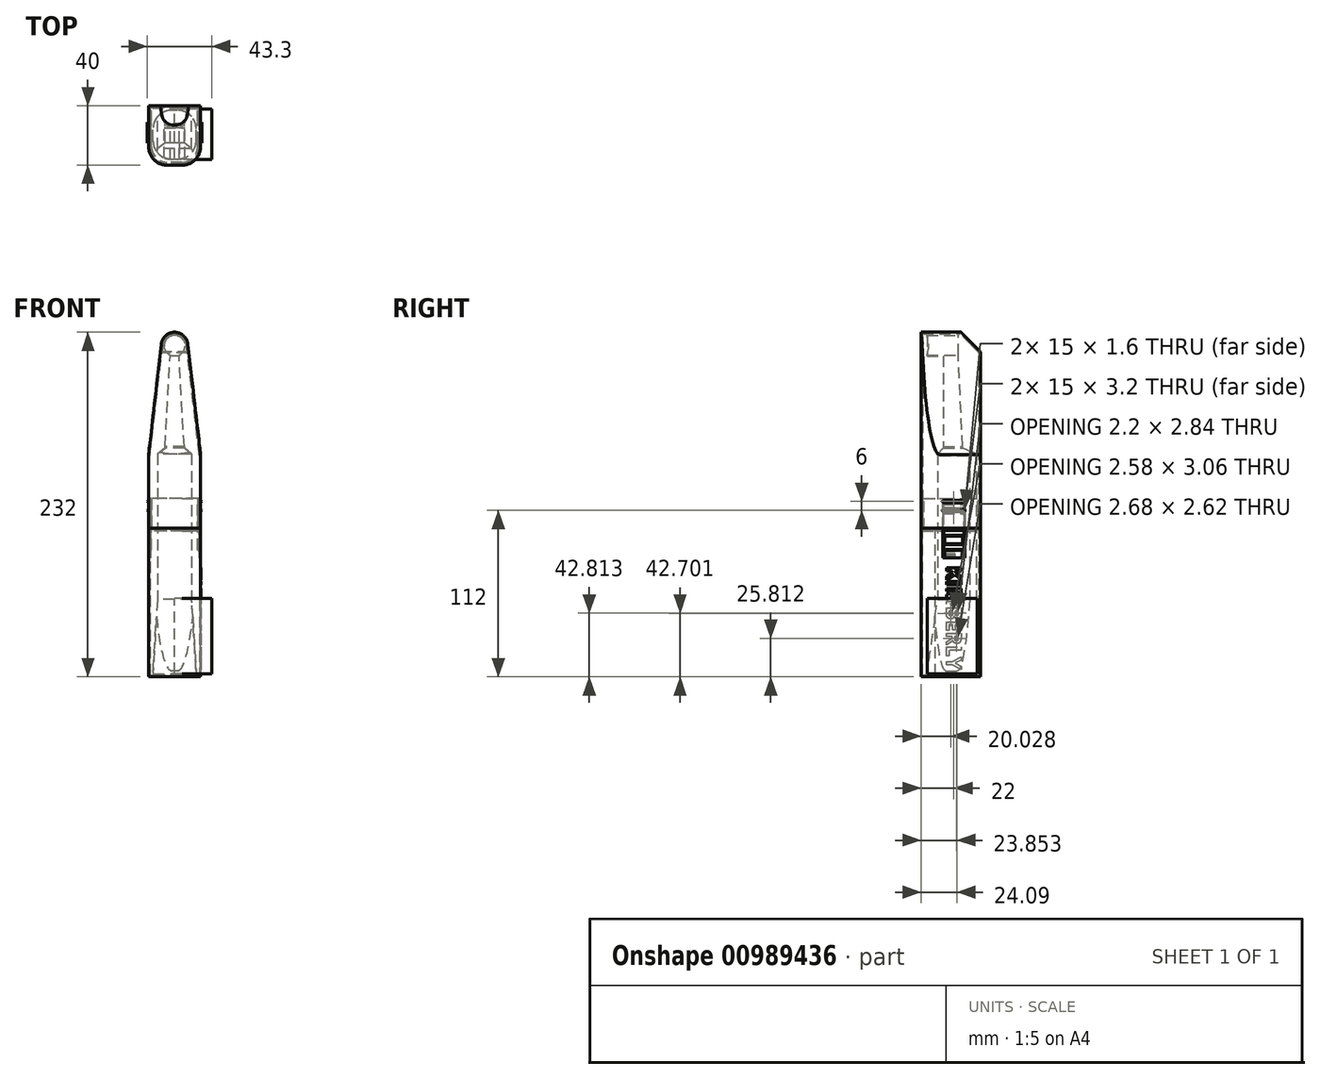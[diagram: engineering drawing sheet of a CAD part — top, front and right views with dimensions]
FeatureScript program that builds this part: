
annotation { "Feature Type Name" : "Feature", "Feature Type Description" : "" }
export const myFeature = defineFeature(function(context is Context, id is Id, definition is map)
    precondition{}
    {
        {
            var Q0;
            Q0=qCreatedBy(makeId("Right.planeOp"),FACE);
            var sketch = newSketch(context, id + "F0", { "sketchPlane" : qUnion([Q0])});
            skLineSegment(sketch, "E0", {"start": v(0, 0) * mm, "end": v(0, 2) * mm});
            skLineSegment(sketch, "E1", {"start": v(0, 2) * mm, "end": v(7, 50) * mm});
            skLineSegment(sketch, "E2", {"start": v(7, 50) * mm, "end": v(7, 148) * mm});
            skLineSegment(sketch, "E3", {"start": v(7, 148) * mm, "end": v(11, 152) * mm});
            skLineSegment(sketch, "E4", {"start": v(11, 152) * mm, "end": v(11, 153) * mm});
            skLineSegment(sketch, "E5", {"start": v(11, 153) * mm, "end": v(11, 214) * mm});
            skLineSegment(sketch, "E6", {"start": v(11, 214) * mm, "end": v(-1, 214) * mm});
            skLineSegment(sketch, "E7", {"start": v(-1, 214) * mm, "end": v(-1, 228) * mm});
            skLineSegment(sketch, "E8", {"start": v(-1, 228) * mm, "end": v(11, 228) * mm});
            skLineSegment(sketch, "E9", {"start": v(11, 228) * mm, "end": v(21, 228) * mm});
            skLineSegment(sketch, "E10", {"start": v(21, 228) * mm, "end": v(21, 214) * mm});
            skLineSegment(sketch, "E11", {"start": v(21, 214) * mm, "end": v(24, 153) * mm});
            skLineSegment(sketch, "E12", {"start": v(24, 153) * mm, "end": v(24, 152) * mm});
            skLineSegment(sketch, "E13", {"start": v(24, 152) * mm, "end": v(33, 148) * mm});
            skLineSegment(sketch, "E14", {"start": v(33, 148) * mm, "end": v(33, 2) * mm});
            skLineSegment(sketch, "E15", {"start": v(33, 2) * mm, "end": v(33, 0) * mm});
            skLineSegment(sketch, "E16", {"start": v(33, 0) * mm, "end": v(0, 0) * mm});
            skLineSegment(sketch, "E17", {"start": v(0, 2) * mm, "end": v(33, 2) * mm, "construction": true});
            skLineSegment(sketch, "E18", {"start": v(11, 153) * mm, "end": v(24, 153) * mm, "construction": true});
            skLineSegment(sketch, "E19", {"start": v(24, 152) * mm, "end": v(11, 152) * mm, "construction": true});
            skLineSegment(sketch, "E20", {"start": v(11, 228) * mm, "end": v(11, 214) * mm, "construction": true});
            skLineSegment(sketch, "E21", {"start": v(7, 148) * mm, "end": v(33, 148) * mm, "construction": true});
            skLineSegment(sketch, "E22", {"start": v(13, 0) * mm, "end": v(13, 10) * mm, "construction": true});
            skLineSegment(sketch, "E23", {"start": v(13, 10) * mm, "end": v(21, 10) * mm, "construction": true});
            skLineSegment(sketch, "E24", {"start": v(21, 10) * mm, "end": v(21, 0) * mm, "construction": true});
            skSolve(sketch);
        }
        {
            var Q0;
            Q0=qCreatedBy(makeId("Front.planeOp"),FACE);
            var sketch = newSketch(context, id + "F1", { "sketchPlane" : qUnion([Q0])});
            skLineSegment(sketch, "E25", {"start": v(14.5, 0) * mm, "end": v(-14.5, 0) * mm});
            skLineSegment(sketch, "E26", {"start": v(-14.5, 0) * mm, "end": v(-14.5, 2) * mm});
            skLineSegment(sketch, "E27", {"start": v(-14.5, 2) * mm, "end": v(-11.5, 50) * mm});
            skLineSegment(sketch, "E28", {"start": v(-11.5, 50) * mm, "end": v(-11.5, 148) * mm});
            skLineSegment(sketch, "E29", {"start": v(-11.5, 148) * mm, "end": v(-6.5, 152) * mm});
            skLineSegment(sketch, "E30", {"start": v(-6.5, 152) * mm, "end": v(-6.5, 153) * mm});
            skLineSegment(sketch, "E31", {"start": v(-6.5, 153) * mm, "end": v(-3, 214.68) * mm});
            skLineSegment(sketch, "E32", {"start": v(-3, 214.68) * mm, "end": v(3, 214.68) * mm});
            skLineSegment(sketch, "E33", {"start": v(3, 214.68) * mm, "end": v(6.5, 153) * mm});
            skLineSegment(sketch, "E34", {"start": v(6.5, 153) * mm, "end": v(6.5, 152) * mm});
            skLineSegment(sketch, "E35", {"start": v(6.5, 152) * mm, "end": v(11.5, 148) * mm});
            skLineSegment(sketch, "E36", {"start": v(11.5, 148) * mm, "end": v(11.5, 50) * mm});
            skLineSegment(sketch, "E37", {"start": v(11.5, 50) * mm, "end": v(14.5, 2) * mm});
            skLineSegment(sketch, "E38", {"start": v(14.5, 2) * mm, "end": v(14.5, 0) * mm});
            skLineSegment(sketch, "E39", {"start": v(14.5, 2) * mm, "end": v(-14.5, 2) * mm, "construction": true});
            skLineSegment(sketch, "E40", {"start": v(-11.5, 50) * mm, "end": v(11.5, 50) * mm, "construction": true});
            skLineSegment(sketch, "E41", {"start": v(-11.5, 148) * mm, "end": v(11.5, 148) * mm, "construction": true});
            skLineSegment(sketch, "E42", {"start": v(6.5, 152) * mm, "end": v(-6.5, 152) * mm, "construction": true});
            skLineSegment(sketch, "E43", {"start": v(-6.5, 153) * mm, "end": v(6.5, 153) * mm, "construction": true});
            skLineSegment(sketch, "E44", {"start": v(0, 0) * mm, "end": v(0, 221) * mm, "construction": true});
            skPoint(sketch, "E44.endSnap0", {"position": v(0, 0) * mm});
            skCircle(sketch, "E45", {"center": v(0, 221) * mm, "radius": 7 * mm});
            skLineSegment(sketch, "E46", {"start": v(-3, 0) * mm, "end": v(-3, 10) * mm, "construction": true});
            skLineSegment(sketch, "E47", {"start": v(-3, 10) * mm, "end": v(3, 10) * mm, "construction": true});
            skLineSegment(sketch, "E48", {"start": v(3, 10) * mm, "end": v(3, 0) * mm, "construction": true});
            skSolve(sketch);
        }
        {
            var Q0;
            Q0 = qSketchRegion(id + "F0", true);
            extrude(context, id + "F2", {"entities" : qUnion([Q0]), "endBound" : BoundingType.SYMMETRIC, "depth" : 50 * mm, "offsetDistance" : 25 * mm});
        }
        {
            var Q0;
            Q0 = qSketchRegion(id + "F1", true);
            extrude(context, id + "F3", {"entities" : qUnion([Q0]), "operationType" : NewBodyOperationType.INTERSECT, "endBound" : BoundingType.SYMMETRIC, "depth" : 100 * mm, "offsetDistance" : 25 * mm});
        }
        {
            var Q0;
            Q0=qCreatedBy(makeId("Top.planeOp"),FACE);
            var sketch = newSketch(context, id + "F4", { "sketchPlane" : qUnion([Q0])});
            skLineSegment(sketch, "E49.bottom", {"start": v(2, 0) * mm, "end": v(-2, 0) * mm});
            skLineSegment(sketch, "E49.top", {"start": v(2, 33) * mm, "end": v(-2, 33) * mm});
            skLineSegment(sketch, "E49.left", {"start": v(14.5, 12.5) * mm, "end": v(14.5, 20.5) * mm});
            skLineSegment(sketch, "E49.right", {"start": v(-14.5, 12.5) * mm, "end": v(-14.5, 20.5) * mm});
            skLineSegment(sketch, "E50", {"start": v(0, 0) * mm, "end": v(0, 33) * mm, "construction": true});
            skPoint(sketch, "E51.visualSharp", {"position": v(-14.5, 33) * mm});
            skArc(sketch, "E51.filletArc", {"start": v(-2, 33) * mm, "mid": v(-10.84, 29.34) * mm, "end": v(-14.5, 20.5) * mm});
            skPoint(sketch, "E52.visualSharp", {"position": v(14.5, 33) * mm});
            skArc(sketch, "E52.filletArc", {"start": v(14.5, 20.5) * mm, "mid": v(10.84, 29.34) * mm, "end": v(2, 33) * mm});
            skPoint(sketch, "E53.visualSharp", {"position": v(-14.5, 0) * mm});
            skArc(sketch, "E53.filletArc", {"start": v(-14.5, 12.5) * mm, "mid": v(-10.84, 3.66) * mm, "end": v(-2, 0) * mm});
            skPoint(sketch, "E54.visualSharp", {"position": v(14.5, 0) * mm});
            skArc(sketch, "E54.filletArc", {"start": v(2, 0) * mm, "mid": v(10.84, 3.66) * mm, "end": v(14.5, 12.5) * mm});
            skSolve(sketch);
        }
        {
            var Q0;
            Q0 = qSketchRegion(id + "F4", true);
            extrude(context, id + "F5", {"entities" : qUnion([Q0]), "operationType" : NewBodyOperationType.INTERSECT, "depth" : 500 * mm, "offsetDistance" : 25 * mm});
        }
        {
            var Q0;
            Q0=qCreatedBy(makeId("Right.planeOp"),FACE);
            var sketch = newSketch(context, id + "F6", { "sketchPlane" : qUnion([Q0])});
            skLineSegment(sketch, "E55", {"start": v(-2, -1) * mm, "end": v(34, -1) * mm});
            skLineSegment(sketch, "E56", {"start": v(34, -1) * mm, "end": v(34, 149) * mm});
            skLineSegment(sketch, "E57", {"start": v(34, 149) * mm, "end": v(22, 229) * mm});
            skLineSegment(sketch, "E58", {"start": v(22, 229) * mm, "end": v(-2, 229) * mm});
            skLineSegment(sketch, "E59", {"start": v(-2, 229) * mm, "end": v(-2, -1) * mm});
            skSolve(sketch);
        }
        {
            var Q0;
            Q0=qCreatedBy(makeId("Right.planeOp"),FACE);
            var sketch = newSketch(context, id + "F7", { "sketchPlane" : qUnion([Q0])});
            skLineSegment(sketch, "E60", {"start": v(-2.8, 118) * mm, "end": v(34.75, 118) * mm});
            skLineSegment(sketch, "E61", {"start": v(34.75, 118) * mm, "end": v(34.75, 98) * mm});
            skLineSegment(sketch, "E62", {"start": v(34.75, 98) * mm, "end": v(36, 98) * mm});
            skLineSegment(sketch, "E63", {"start": v(36, 98) * mm, "end": v(36, -2) * mm});
            skLineSegment(sketch, "E64", {"start": v(36, -2) * mm, "end": v(-4, -2) * mm});
            skLineSegment(sketch, "E65", {"start": v(-4, -2) * mm, "end": v(-4, 98) * mm});
            skLineSegment(sketch, "E66", {"start": v(-4, 98) * mm, "end": v(-2.8, 98) * mm});
            skLineSegment(sketch, "E67", {"start": v(-2.8, 98) * mm, "end": v(-2.8, 118) * mm});
            skSolve(sketch);
        }
        {
            var Q0;
            Q0=qCreatedBy(makeId("Right.planeOp"),FACE);
            var sketch = newSketch(context, id + "F8", { "sketchPlane" : qUnion([Q0])});
            skLineSegment(sketch, "E68", {"start": v(-2, 118) * mm, "end": v(34, 118) * mm});
            skLineSegment(sketch, "E69", {"start": v(34, 118) * mm, "end": v(34, 97.2) * mm});
            skLineSegment(sketch, "E70", {"start": v(34, 97.2) * mm, "end": v(35.2, 97.2) * mm, "construction": true});
            skLineSegment(sketch, "E71", {"start": v(35.2, 97.2) * mm, "end": v(35.2, 96) * mm, "construction": true});
            skLineSegment(sketch, "E72", {"start": v(35.2, -1) * mm, "end": v(-3.2, -1) * mm});
            skLineSegment(sketch, "E73", {"start": v(-3.2, -1) * mm, "end": v(-3.2, 96) * mm});
            skLineSegment(sketch, "E74", {"start": v(-3.2, 97.2) * mm, "end": v(-2, 97.2) * mm, "construction": true});
            skLineSegment(sketch, "E75", {"start": v(-2, 97.2) * mm, "end": v(-2, 118) * mm});
            skLineSegment(sketch, "E76", {"start": v(-3.2, 96) * mm, "end": v(-3.2, 97.2) * mm, "construction": true});
            skLineSegment(sketch, "E77", {"start": v(35.2, 96) * mm, "end": v(35.2, -1) * mm});
            skLineSegment(sketch, "E78", {"start": v(-3.2, 96) * mm, "end": v(-2, 97.2) * mm});
            skLineSegment(sketch, "E79", {"start": v(35.2, 96) * mm, "end": v(34, 97.2) * mm});
            skSolve(sketch);
        }
        {
            var Q0;
            Q0=qCreatedBy(makeId("Right.planeOp"),FACE);
            var sketch = newSketch(context, id + "F9", { "sketchPlane" : qUnion([Q0])});
            skLineSegment(sketch, "E80", {"start": v(-4, 98) * mm, "end": v(-4, 230) * mm});
            skLineSegment(sketch, "E81", {"start": v(-4, 230) * mm, "end": v(22.86, 230) * mm});
            skLineSegment(sketch, "E82", {"start": v(22.86, 230) * mm, "end": v(36, 142.4) * mm, "construction": true});
            skLineSegment(sketch, "E83", {"start": v(36, 142.4) * mm, "end": v(36, 98) * mm});
            skLineSegment(sketch, "E84", {"start": v(36, 98) * mm, "end": v(-4, 98) * mm});
            skLineSegment(sketch, "E85", {"start": v(22.86, 230) * mm, "end": v(36, 216.86) * mm});
            skLineSegment(sketch, "E86", {"start": v(36, 216.86) * mm, "end": v(36, 142.4) * mm});
            skSolve(sketch);
        }
        {
            var Q0;
            Q0=qCreatedBy(makeId("Right.planeOp"),FACE);
            var sketch = newSketch(context, id + "F10", { "sketchPlane" : qUnion([Q0])});
            skLineSegment(sketch, "E87", {"start": v(22.17, 229.2) * mm, "end": v(35.2, 142.35) * mm, "construction": true});
            skLineSegment(sketch, "E88", {"start": v(35.2, 142.35) * mm, "end": v(35.2, 98) * mm});
            skLineSegment(sketch, "E89", {"start": v(35.2, 98) * mm, "end": v(-3.2, 98) * mm});
            skLineSegment(sketch, "E90", {"start": v(22.17, 229.2) * mm, "end": v(-3.2, 229.2) * mm});
            skLineSegment(sketch, "E91", {"start": v(-3.2, 229.2) * mm, "end": v(-3.2, 98) * mm});
            skLineSegment(sketch, "E92", {"start": v(35.2, 142.35) * mm, "end": v(35.2, 216.17) * mm});
            skLineSegment(sketch, "E93", {"start": v(35.2, 216.17) * mm, "end": v(22.17, 229.2) * mm});
            skSolve(sketch);
        }
        {
            var Q0;
            Q0=qCreatedBy(makeId("Front.planeOp"),FACE);
            var sketch = newSketch(context, id + "F11", { "sketchPlane" : qUnion([Q0])});
            skLineSegment(sketch, "E94", {"start": v(-15.5, 149) * mm, "end": v(-15.5, -1) * mm});
            skLineSegment(sketch, "E95", {"start": v(-15.5, -1) * mm, "end": v(15.5, -1) * mm});
            skLineSegment(sketch, "E96", {"start": v(15.5, -1) * mm, "end": v(15.5, 149) * mm});
            skLineSegment(sketch, "E97", {"start": v(15.5, 149) * mm, "end": v(-15.5, 149) * mm});
            skLineSegment(sketch, "E98", {"start": v(15.5, 149) * mm, "end": v(12.5, 154) * mm});
            skLineSegment(sketch, "E99", {"start": v(-15.5, 149) * mm, "end": v(-12.5, 154) * mm});
            skLineSegment(sketch, "E100", {"start": v(-12.5, 154) * mm, "end": v(12.5, 154) * mm});
            skLineSegment(sketch, "E101", {"start": v(-12.5, 154) * mm, "end": v(-7.98, 221.53) * mm});
            skLineSegment(sketch, "E102", {"start": v(12.5, 154) * mm, "end": v(7.98, 221.53) * mm});
            skArc(sketch, "E103", {"start": v(-7.98, 221.53) * mm, "mid": v(0, 229) * mm, "end": v(7.98, 221.53) * mm});
            skSolve(sketch);
        }
        {
            var Q0;
            Q0=qCreatedBy(makeId("Front.planeOp"),FACE);
            var sketch = newSketch(context, id + "F12", { "sketchPlane" : qUnion([Q0])});
            skLineSegment(sketch, "E104", {"start": v(-16.3, 118) * mm, "end": v(-16.3, 98) * mm});
            skLineSegment(sketch, "E105", {"start": v(-16.3, 98) * mm, "end": v(-17.5, 98) * mm});
            skLineSegment(sketch, "E106", {"start": v(-17.5, 98) * mm, "end": v(-17.5, -2) * mm});
            skLineSegment(sketch, "E107", {"start": v(-17.5, -2) * mm, "end": v(17.5, -2) * mm});
            skLineSegment(sketch, "E108", {"start": v(17.5, -2) * mm, "end": v(17.5, 98) * mm});
            skLineSegment(sketch, "E109", {"start": v(17.5, 98) * mm, "end": v(16.3, 98) * mm});
            skLineSegment(sketch, "E110", {"start": v(16.3, 98) * mm, "end": v(16.3, 118) * mm});
            skLineSegment(sketch, "E111", {"start": v(16.3, 118) * mm, "end": v(-16.3, 118) * mm});
            skSolve(sketch);
        }
        {
            var Q0;
            Q0=qCreatedBy(makeId("Front.planeOp"),FACE);
            var sketch = newSketch(context, id + "F13", { "sketchPlane" : qUnion([Q0])});
            skLineSegment(sketch, "E112", {"start": v(-15.5, 118) * mm, "end": v(-15.5, 97.2) * mm});
            skLineSegment(sketch, "E113", {"start": v(-15.5, 97.2) * mm, "end": v(-16.3, 97.2) * mm, "construction": true});
            skLineSegment(sketch, "E114", {"start": v(-16.3, 97.2) * mm, "end": v(-16.3, 96.4) * mm, "construction": true});
            skLineSegment(sketch, "E115", {"start": v(-16.3, -1) * mm, "end": v(16.7, -1) * mm});
            skLineSegment(sketch, "E116", {"start": v(16.7, -1) * mm, "end": v(16.7, 96) * mm});
            skLineSegment(sketch, "E117", {"start": v(16.7, 97.2) * mm, "end": v(15.5, 97.2) * mm, "construction": true});
            skLineSegment(sketch, "E118", {"start": v(15.5, 97.2) * mm, "end": v(15.5, 118) * mm});
            skLineSegment(sketch, "E119", {"start": v(15.5, 118) * mm, "end": v(-15.5, 118) * mm});
            skLineSegment(sketch, "E120", {"start": v(-16.3, 96.4) * mm, "end": v(-16.3, -1) * mm});
            skLineSegment(sketch, "E121", {"start": v(16.7, 96) * mm, "end": v(16.7, 97.2) * mm, "construction": true});
            skLineSegment(sketch, "E122", {"start": v(-16.3, 96.4) * mm, "end": v(-15.5, 97.2) * mm});
            skLineSegment(sketch, "E123", {"start": v(16.7, 96) * mm, "end": v(15.5, 97.2) * mm});
            skSolve(sketch);
        }
        {
            var Q0;
            Q0=qCreatedBy(makeId("Front.planeOp"),FACE);
            var sketch = newSketch(context, id + "F14", { "sketchPlane" : qUnion([Q0])});
            skLineSegment(sketch, "E124", {"start": v(-17.5, 98) * mm, "end": v(17.5, 98) * mm});
            skLineSegment(sketch, "E125", {"start": v(17.5, 98) * mm, "end": v(17.5, 147.61) * mm});
            skLineSegment(sketch, "E126", {"start": v(17.5, 147.61) * mm, "end": v(13.48, 154.3) * mm, "construction": true});
            skLineSegment(sketch, "E127", {"start": v(13.48, 154.3) * mm, "end": v(8.98, 221.6) * mm, "construction": true});
            skLineSegment(sketch, "E128", {"start": v(-17.5, 98) * mm, "end": v(-17.5, 147.61) * mm});
            skLineSegment(sketch, "E129", {"start": v(-17.5, 147.61) * mm, "end": v(-13.48, 154.3) * mm, "construction": true});
            skLineSegment(sketch, "E130", {"start": v(-13.48, 154.3) * mm, "end": v(-8.98, 221.6) * mm, "construction": true});
            skArc(sketch, "E131", {"start": v(-8.98, 221.6) * mm, "mid": v(-8.96, 221.81) * mm, "end": v(-8.94, 222.03) * mm, "construction": true});
            skArc(sketch, "E132", {"start": v(8.94, 222.03) * mm, "mid": v(8.96, 221.81) * mm, "end": v(8.98, 221.6) * mm, "construction": true});
            skArc(sketch, "E133", {"start": v(-8.94, 222.03) * mm, "mid": v(0, 230) * mm, "end": v(8.94, 222.03) * mm});
            skLineSegment(sketch, "E134", {"start": v(-8.94, 222.03) * mm, "end": v(-17.5, 147.61) * mm});
            skLineSegment(sketch, "E135", {"start": v(8.94, 222.03) * mm, "end": v(17.5, 147.61) * mm});
            skSolve(sketch);
        }
        {
            var Q0;
            Q0=qCreatedBy(makeId("Front.planeOp"),FACE);
            var sketch = newSketch(context, id + "F15", { "sketchPlane" : qUnion([Q0])});
            skLineSegment(sketch, "E136", {"start": v(16.7, 98) * mm, "end": v(16.7, 147) * mm});
            skLineSegment(sketch, "E137", {"start": v(16.7, 147) * mm, "end": v(12.5, 154) * mm, "construction": true});
            skLineSegment(sketch, "E138", {"start": v(12.5, 154) * mm, "end": v(7.98, 221.53) * mm, "construction": true});
            skLineSegment(sketch, "E139", {"start": v(16.7, 98) * mm, "end": v(-16.7, 98) * mm});
            skLineSegment(sketch, "E140", {"start": v(-16.7, 98) * mm, "end": v(-16.7, 147) * mm});
            skLineSegment(sketch, "E141", {"start": v(-16.7, 147) * mm, "end": v(-12.5, 154) * mm, "construction": true});
            skLineSegment(sketch, "E142", {"start": v(-12.5, 154) * mm, "end": v(-7.98, 221.53) * mm, "construction": true});
            skArc(sketch, "E143.0", {"start": v(-7.98, 221.53) * mm, "mid": v(-7.97, 221.73) * mm, "end": v(-7.95, 221.93) * mm, "construction": true});
            skArc(sketch, "E144", {"start": v(-7.95, 221.93) * mm, "mid": v(0, 229) * mm, "end": v(7.95, 221.93) * mm});
            skArc(sketch, "E145", {"start": v(7.95, 221.93) * mm, "mid": v(7.97, 221.73) * mm, "end": v(7.98, 221.53) * mm, "construction": true});
            skLineSegment(sketch, "E146", {"start": v(-16.7, 147) * mm, "end": v(-7.95, 221.93) * mm});
            skLineSegment(sketch, "E147", {"start": v(16.7, 147) * mm, "end": v(7.95, 221.93) * mm});
            skSolve(sketch);
        }
        {
            var Q0;
            Q0 = qSketchRegion(id + "F8", true);
            var Q1;
            Q1 = qSketchRegion(id + "F7", true);
            var Q2;
            Q2 = qSketchRegion(id + "F9", true);
            var Q3;
            Q3 = qSketchRegion(id + "F10", true);
            extrude(context, id + "F16", {"entities" : qUnion([Q0, Q1, Q2, Q3]), "endBound" : BoundingType.SYMMETRIC, "depth" : 50 * mm, "offsetDistance" : 25 * mm});
        }
        {
            var Q0;
            Q0 = qSketchRegion(id + "F12", true);
            var Q1;
            Q1 = qSketchRegion(id + "F13", true);
            var Q2;
            Q2 = qSketchRegion(id + "F14", true);
            var Q3;
            Q3 = qSketchRegion(id + "F15", true);
            extrude(context, id + "F17", {"entities" : qUnion([Q0, Q1, Q2, Q3]), "endBound" : BoundingType.SYMMETRIC, "depth" : 100 * mm, "offsetDistance" : 25 * mm});
        }
        {
            var Q0;
            Q0=makeQuery(id+"F16.opExtrude","SWEPT_BODY",BODY,{"disambiguationData":[OSD([sQuery(id+"F9.wireOp",EDGE,"E80"),sQuery(id+"F9.wireOp",EDGE,"E81"),sQuery(id+"F9.wireOp",EDGE,"E82"),sQuery(id+"F9.wireOp",EDGE,"E83"),sQuery(id+"F9.wireOp",EDGE,"E84")])]});
            var Q1;
            Q1=makeQuery(id+"F17.opExtrude","SWEPT_BODY",BODY,{"disambiguationData":[OSD([sQuery(id+"F14.wireOp",EDGE,"E124"),sQuery(id+"F14.wireOp",EDGE,"E125"),sQuery(id+"F14.wireOp",EDGE,"E126"),sQuery(id+"F14.wireOp",EDGE,"E127"),sQuery(id+"F14.wireOp",EDGE,"E128"),sQuery(id+"F14.wireOp",EDGE,"E129"),sQuery(id+"F14.wireOp",EDGE,"E130"),sQuery(id+"F14.wireOp",EDGE,"E131")])]});
            booleanBodies(context, id + "F18", {"operationType" : BooleanOperationType.INTERSECTION, "tools" : qUnion([Q0, Q1])});
        }
        {
            var Q0;
            Q0=makeQuery(id+"F16.opExtrude","SWEPT_BODY",BODY,{"disambiguationData":[OSD([sQuery(id+"F10.wireOp",EDGE,"E87"),sQuery(id+"F10.wireOp",EDGE,"E88"),sQuery(id+"F10.wireOp",EDGE,"W1tJQCin-OEPZ-rTFv-T9rl-aR893KYHEF2I"),sQuery(id+"F10.wireOp",EDGE,"p4VvJ2oT-vXJB-r7VE-dOSy-3ZbD9Ky7NWsE"),sQuery(id+"F10.wireOp",EDGE,"E89"),sQuery(id+"F10.wireOp",EDGE,"E90"),sQuery(id+"F10.wireOp",EDGE,"E91"),sQuery(id+"F10.wireOp",EDGE,"Jw9tlb3h-XCuH-rQZM-sFqi-2SsdOfsYjVly"),sQuery(id+"F10.wireOp",EDGE,"6l9JFlLI-izCi-OQrv-6RJF-6f1TNNtmB2PI")])]});
            var Q1;
            Q1=makeQuery(id+"F17.opExtrude","SWEPT_BODY",BODY,{"disambiguationData":[OSD([sQuery(id+"F15.wireOp",EDGE,"7L5QcHba-olP2-1ewQ-sv9H-xwOJC43mXpUe"),sQuery(id+"F15.wireOp",EDGE,"X5xDe7kA-WwP7-RUg3-9NvY-zUZtMzpXXzgn"),sQuery(id+"F15.wireOp",EDGE,"E136"),sQuery(id+"F15.wireOp",EDGE,"E137"),sQuery(id+"F15.wireOp",EDGE,"E138"),sQuery(id+"F15.wireOp",EDGE,"E139"),sQuery(id+"F15.wireOp",EDGE,"owWedUeD-2nhG-T1I6-ZLYN-mTq45OQbvkC9"),sQuery(id+"F15.wireOp",EDGE,"yBYLwaW9-tenq-o43d-Rucl-tS4PAnVahWbH"),sQuery(id+"F15.wireOp",EDGE,"E140"),sQuery(id+"F15.wireOp",EDGE,"E141"),sQuery(id+"F15.wireOp",EDGE,"E142"),sQuery(id+"F15.wireOp",EDGE,"E143.0")])]});
            booleanBodies(context, id + "F19", {"operationType" : BooleanOperationType.INTERSECTION, "tools" : qUnion([Q0, Q1])});
        }
        {
            var Q0;
            Q0=makeQuery(id+"F17.opExtrude","SWEPT_BODY",BODY,{"disambiguationData":[OSD([sQuery(id+"F12.wireOp",EDGE,"E104"),sQuery(id+"F12.wireOp",EDGE,"E105"),sQuery(id+"F12.wireOp",EDGE,"E106"),sQuery(id+"F12.wireOp",EDGE,"E107"),sQuery(id+"F12.wireOp",EDGE,"E108"),sQuery(id+"F12.wireOp",EDGE,"E109"),sQuery(id+"F12.wireOp",EDGE,"E110"),sQuery(id+"F12.wireOp",EDGE,"E111")])]});
            var Q1;
            Q1=makeQuery(id+"F16.opExtrude","SWEPT_BODY",BODY,{"disambiguationData":[OSD([sQuery(id+"F7.wireOp",EDGE,"E60"),sQuery(id+"F7.wireOp",EDGE,"E61"),sQuery(id+"F7.wireOp",EDGE,"E62"),sQuery(id+"F7.wireOp",EDGE,"E63"),sQuery(id+"F7.wireOp",EDGE,"E64"),sQuery(id+"F7.wireOp",EDGE,"E65"),sQuery(id+"F7.wireOp",EDGE,"E66"),sQuery(id+"F7.wireOp",EDGE,"E67")])]});
            booleanBodies(context, id + "F20", {"operationType" : BooleanOperationType.INTERSECTION, "tools" : qUnion([Q0, Q1])});
        }
        {
            var Q0;
            Q0=makeQuery(id+"F17.opExtrude","SWEPT_BODY",BODY,{"disambiguationData":[OSD([sQuery(id+"F13.wireOp",EDGE,"E112"),sQuery(id+"F13.wireOp",EDGE,"E113"),sQuery(id+"F13.wireOp",EDGE,"E114"),sQuery(id+"F13.wireOp",EDGE,"E115"),sQuery(id+"F13.wireOp",EDGE,"E116"),sQuery(id+"F13.wireOp",EDGE,"E117"),sQuery(id+"F13.wireOp",EDGE,"E118"),sQuery(id+"F13.wireOp",EDGE,"E119")])]});
            var Q1;
            Q1=makeQuery(id+"F16.opExtrude","SWEPT_BODY",BODY,{"disambiguationData":[OSD([sQuery(id+"F8.wireOp",EDGE,"E68"),sQuery(id+"F8.wireOp",EDGE,"E69"),sQuery(id+"F8.wireOp",EDGE,"E70"),sQuery(id+"F8.wireOp",EDGE,"E71"),sQuery(id+"F8.wireOp",EDGE,"E72"),sQuery(id+"F8.wireOp",EDGE,"E73"),sQuery(id+"F8.wireOp",EDGE,"E74"),sQuery(id+"F8.wireOp",EDGE,"E75")])]});
            booleanBodies(context, id + "F21", {"operationType" : BooleanOperationType.INTERSECTION, "tools" : qUnion([Q0, Q1])});
        }
        {
            assignVariable(context, id + "F22", {"name" : "Round_trans", "anyValue" : 8.5});
        }
        {
            var Q0;
            Q0=qCreatedBy(makeId("Front.planeOp"),FACE);
            var sketch = newSketch(context, id + "F23", { "sketchPlane" : qUnion([Q0])});
            skLineSegment(sketch, "E148", {"start": v(16.7, 248) * mm, "end": v(41.7, 248) * mm});
            skLineSegment(sketch, "E149", {"start": v(41.7, 248) * mm, "end": v(41.7, 98) * mm});
            skLineSegment(sketch, "E150", {"start": v(41.7, 98) * mm, "end": v(16.7, 98) * mm});
            skLineSegment(sketch, "E151", {"start": v(16.7, 248) * mm, "end": v(5, 248) * mm, "construction": true});
            skLineSegment(sketch, "E152", {"start": v(5, 98) * mm, "end": v(16.7, 98) * mm, "construction": true});
            skLineSegment(sketch, "E153", {"start": v(5, 248) * mm, "end": v(5, 98) * mm});
            skLineSegment(sketch, "E154", {"start": v(16.7, 248) * mm, "end": v(16.7, 98) * mm});
            skSolve(sketch);
        }
        {
            var Q0;
            Q0=qCreatedBy(makeId("Front.planeOp"),FACE);
            var sketch = newSketch(context, id + "F24", { "sketchPlane" : qUnion([Q0])});
            skLineSegment(sketch, "E155.0", {"start": v(17.5, 98) * mm, "end": v(17.5, 147.61) * mm});
            skLineSegment(sketch, "E156", {"start": v(17.5, 147.61) * mm, "end": v(17.5, 248) * mm});
            skLineSegment(sketch, "E157", {"start": v(17.5, 248) * mm, "end": v(41.7, 248) * mm});
            skLineSegment(sketch, "E158", {"start": v(41.7, 248) * mm, "end": v(41.7, 98) * mm});
            skLineSegment(sketch, "E159", {"start": v(41.7, 98) * mm, "end": v(17.5, 98) * mm});
            skSolve(sketch);
        }
        {
            var Q0;
            Q0 = qSketchRegion(id + "F23", true);
            var Q1;
            Q1 = qSketchRegion(id + "F24", true);
            var Q2;
            Q2=sQuery(id+"F23.wireOp",EDGE,"E153");
            revolve(context, id + "F25", {"surfaceOperationType" : NewSurfaceOperationType.NEW, "entities" : qUnion([Q0, Q1]), "axis" : qUnion([Q2]), "revolveType" : RevolveType.ONE_DIRECTION, "angle" : 90 * degree});
        }
        {
            var Q0;
            Q0=makeQuery(id+"F25.opRevolve","SWEPT_BODY",BODY,{"disambiguationData":[OSD([sQuery(id+"F23.wireOp",EDGE,"6764aa32-18b0-40c9-89ac-cbd8d3af00d8.0"),sQuery(id+"F23.wireOp",EDGE,"6764aa32-18b0-40c9-89ac-cbd8d3af00d8.1"),sQuery(id+"F23.wireOp",EDGE,"6764aa32-18b0-40c9-89ac-cbd8d3af00d8.2"),sQuery(id+"F23.wireOp",EDGE,"7vJRygaZ-DCmo-56W3-YPe7-tXBA3UdhYIz2"),sQuery(id+"F23.wireOp",EDGE,"E148"),sQuery(id+"F23.wireOp",EDGE,"E149"),sQuery(id+"F23.wireOp",EDGE,"E150")])]});
            var Q1;
            Q1=makeQuery(id+"F25.opRevolve","SWEPT_BODY",BODY,{"disambiguationData":[OSD([sQuery(id+"F24.wireOp",EDGE,"E155.0"),sQuery(id+"F24.wireOp",EDGE,"E156"),sQuery(id+"F24.wireOp",EDGE,"E157"),sQuery(id+"F24.wireOp",EDGE,"E158"),sQuery(id+"F24.wireOp",EDGE,"E159")])]});
            transform(context, id + "F26", {"entities" : qUnion([Q0, Q1]), "transformType" : TransformType.TRANSLATION_3D, "dx" : 0 * mm, "dy" : getVariable(context, 'Round_trans') * mm, "dz" : 0 * mm, "makeCopy" : false});
        }
        {
            var Q0;
            Q0=makeQuery(id+"F25.opRevolve","SWEPT_BODY",BODY,{"disambiguationData":[OSD([sQuery(id+"F24.wireOp",EDGE,"E155.0"),sQuery(id+"F24.wireOp",EDGE,"E156"),sQuery(id+"F24.wireOp",EDGE,"E157"),sQuery(id+"F24.wireOp",EDGE,"E158"),sQuery(id+"F24.wireOp",EDGE,"E159")])]});
            var Q1;
            Q1=makeQuery(id+"F25.opRevolve","SWEPT_BODY",BODY,{"disambiguationData":[OSD([sQuery(id+"F23.wireOp",EDGE,"6764aa32-18b0-40c9-89ac-cbd8d3af00d8.0"),sQuery(id+"F23.wireOp",EDGE,"6764aa32-18b0-40c9-89ac-cbd8d3af00d8.1"),sQuery(id+"F23.wireOp",EDGE,"6764aa32-18b0-40c9-89ac-cbd8d3af00d8.2"),sQuery(id+"F23.wireOp",EDGE,"7vJRygaZ-DCmo-56W3-YPe7-tXBA3UdhYIz2"),sQuery(id+"F23.wireOp",EDGE,"E148"),sQuery(id+"F23.wireOp",EDGE,"E149"),sQuery(id+"F23.wireOp",EDGE,"E150")])]});
            var Q2;
            Q2=qCreatedBy(makeId("Right.planeOp"),FACE);
            mirror(context, id + "F27", {"entities" : qUnion([Q0, Q1]), "mirrorPlane" : qUnion([Q2])});
        }
        {
            var Q0;
            Q0=makeQuery(id+"F25.opRevolve","SWEPT_BODY",BODY,{"disambiguationData":[OSD([sQuery(id+"F23.wireOp",EDGE,"6764aa32-18b0-40c9-89ac-cbd8d3af00d8.0"),sQuery(id+"F23.wireOp",EDGE,"6764aa32-18b0-40c9-89ac-cbd8d3af00d8.1"),sQuery(id+"F23.wireOp",EDGE,"6764aa32-18b0-40c9-89ac-cbd8d3af00d8.2"),sQuery(id+"F23.wireOp",EDGE,"7vJRygaZ-DCmo-56W3-YPe7-tXBA3UdhYIz2"),sQuery(id+"F23.wireOp",EDGE,"E148"),sQuery(id+"F23.wireOp",EDGE,"E149"),sQuery(id+"F23.wireOp",EDGE,"E150")])]});
            var Q1;
            Q1=makeQuery(id+"F27.opPattern","COPY",BODY,{"derivedFrom":makeQuery(id+"F25.opRevolve","SWEPT_BODY",BODY,{"disambiguationData":[OSD([sQuery(id+"F23.wireOp",EDGE,"6764aa32-18b0-40c9-89ac-cbd8d3af00d8.0"),sQuery(id+"F23.wireOp",EDGE,"6764aa32-18b0-40c9-89ac-cbd8d3af00d8.1"),sQuery(id+"F23.wireOp",EDGE,"6764aa32-18b0-40c9-89ac-cbd8d3af00d8.2"),sQuery(id+"F23.wireOp",EDGE,"7vJRygaZ-DCmo-56W3-YPe7-tXBA3UdhYIz2"),sQuery(id+"F23.wireOp",EDGE,"E148"),sQuery(id+"F23.wireOp",EDGE,"E149"),sQuery(id+"F23.wireOp",EDGE,"E150")])]}),"instanceName":"1"});
            var Q2;
            Q2=makeQuery(id+"F19.opBoolean","INTERSECT",BODY,{"derivedFrom":[makeQuery(id+"F16.opExtrude","SWEPT_BODY",BODY,{"disambiguationData":[OSD([sQuery(id+"F10.wireOp",EDGE,"E87"),sQuery(id+"F10.wireOp",EDGE,"E88"),sQuery(id+"F10.wireOp",EDGE,"W1tJQCin-OEPZ-rTFv-T9rl-aR893KYHEF2I"),sQuery(id+"F10.wireOp",EDGE,"p4VvJ2oT-vXJB-r7VE-dOSy-3ZbD9Ky7NWsE"),sQuery(id+"F10.wireOp",EDGE,"E89"),sQuery(id+"F10.wireOp",EDGE,"E90"),sQuery(id+"F10.wireOp",EDGE,"E91"),sQuery(id+"F10.wireOp",EDGE,"Jw9tlb3h-XCuH-rQZM-sFqi-2SsdOfsYjVly"),sQuery(id+"F10.wireOp",EDGE,"6l9JFlLI-izCi-OQrv-6RJF-6f1TNNtmB2PI")])]}),makeQuery(id+"F17.opExtrude","SWEPT_BODY",BODY,{"disambiguationData":[OSD([sQuery(id+"F15.wireOp",EDGE,"7L5QcHba-olP2-1ewQ-sv9H-xwOJC43mXpUe"),sQuery(id+"F15.wireOp",EDGE,"X5xDe7kA-WwP7-RUg3-9NvY-zUZtMzpXXzgn"),sQuery(id+"F15.wireOp",EDGE,"E136"),sQuery(id+"F15.wireOp",EDGE,"E139"),sQuery(id+"F15.wireOp",EDGE,"owWedUeD-2nhG-T1I6-ZLYN-mTq45OQbvkC9"),sQuery(id+"F15.wireOp",EDGE,"yBYLwaW9-tenq-o43d-Rucl-tS4PAnVahWbH"),sQuery(id+"F15.wireOp",EDGE,"E140"),sQuery(id+"F15.wireOp",EDGE,"E144"),sQuery(id+"F15.wireOp",EDGE,"E146"),sQuery(id+"F15.wireOp",EDGE,"E147")])]})]});
            booleanBodies(context, id + "F28", {"operationType" : BooleanOperationType.SUBTRACTION, "tools" : qUnion([Q0, Q1]), "targets" : qUnion([Q2])});
        }
        {
            var Q0;
            Q0=makeQuery(id+"F25.opRevolve","SWEPT_BODY",BODY,{"disambiguationData":[OSD([sQuery(id+"F24.wireOp",EDGE,"E155.0"),sQuery(id+"F24.wireOp",EDGE,"E156"),sQuery(id+"F24.wireOp",EDGE,"E157"),sQuery(id+"F24.wireOp",EDGE,"E158"),sQuery(id+"F24.wireOp",EDGE,"E159")])]});
            var Q1;
            Q1=makeQuery(id+"F27.opPattern","COPY",BODY,{"derivedFrom":makeQuery(id+"F25.opRevolve","SWEPT_BODY",BODY,{"disambiguationData":[OSD([sQuery(id+"F24.wireOp",EDGE,"E155.0"),sQuery(id+"F24.wireOp",EDGE,"E156"),sQuery(id+"F24.wireOp",EDGE,"E157"),sQuery(id+"F24.wireOp",EDGE,"E158"),sQuery(id+"F24.wireOp",EDGE,"E159")])]}),"instanceName":"1"});
            var Q2;
            Q2=makeQuery(id+"F18.opBoolean","INTERSECT",BODY,{"derivedFrom":[makeQuery(id+"F16.opExtrude","SWEPT_BODY",BODY,{"disambiguationData":[OSD([sQuery(id+"F9.wireOp",EDGE,"E80"),sQuery(id+"F9.wireOp",EDGE,"E81"),sQuery(id+"F9.wireOp",EDGE,"E82"),sQuery(id+"F9.wireOp",EDGE,"E83"),sQuery(id+"F9.wireOp",EDGE,"E84")])]}),makeQuery(id+"F17.opExtrude","SWEPT_BODY",BODY,{"disambiguationData":[OSD([sQuery(id+"F14.wireOp",EDGE,"E124"),sQuery(id+"F14.wireOp",EDGE,"E125"),sQuery(id+"F14.wireOp",EDGE,"E128"),sQuery(id+"F14.wireOp",EDGE,"E133"),sQuery(id+"F14.wireOp",EDGE,"E134"),sQuery(id+"F14.wireOp",EDGE,"E135")])]})]});
            booleanBodies(context, id + "F29", {"operationType" : BooleanOperationType.SUBTRACTION, "tools" : qUnion([Q0, Q1]), "targets" : qUnion([Q2])});
        }
        {
            var Q0;
            Q0=makeQuery(id+"F19.opBoolean","INTERSECT",BODY,{"derivedFrom":[makeQuery(id+"F16.opExtrude","SWEPT_BODY",BODY,{"disambiguationData":[OSD([sQuery(id+"F10.wireOp",EDGE,"E87"),sQuery(id+"F10.wireOp",EDGE,"E88"),sQuery(id+"F10.wireOp",EDGE,"W1tJQCin-OEPZ-rTFv-T9rl-aR893KYHEF2I"),sQuery(id+"F10.wireOp",EDGE,"p4VvJ2oT-vXJB-r7VE-dOSy-3ZbD9Ky7NWsE"),sQuery(id+"F10.wireOp",EDGE,"E89"),sQuery(id+"F10.wireOp",EDGE,"E90"),sQuery(id+"F10.wireOp",EDGE,"E91"),sQuery(id+"F10.wireOp",EDGE,"Jw9tlb3h-XCuH-rQZM-sFqi-2SsdOfsYjVly"),sQuery(id+"F10.wireOp",EDGE,"6l9JFlLI-izCi-OQrv-6RJF-6f1TNNtmB2PI")])]}),makeQuery(id+"F17.opExtrude","SWEPT_BODY",BODY,{"disambiguationData":[OSD([sQuery(id+"F15.wireOp",EDGE,"7L5QcHba-olP2-1ewQ-sv9H-xwOJC43mXpUe"),sQuery(id+"F15.wireOp",EDGE,"X5xDe7kA-WwP7-RUg3-9NvY-zUZtMzpXXzgn"),sQuery(id+"F15.wireOp",EDGE,"E136"),sQuery(id+"F15.wireOp",EDGE,"E139"),sQuery(id+"F15.wireOp",EDGE,"owWedUeD-2nhG-T1I6-ZLYN-mTq45OQbvkC9"),sQuery(id+"F15.wireOp",EDGE,"yBYLwaW9-tenq-o43d-Rucl-tS4PAnVahWbH"),sQuery(id+"F15.wireOp",EDGE,"E140"),sQuery(id+"F15.wireOp",EDGE,"E144"),sQuery(id+"F15.wireOp",EDGE,"E146"),sQuery(id+"F15.wireOp",EDGE,"E147")])]})]});
            var Q1;
            Q1=makeQuery(id+"F18.opBoolean","INTERSECT",BODY,{"derivedFrom":[makeQuery(id+"F16.opExtrude","SWEPT_BODY",BODY,{"disambiguationData":[OSD([sQuery(id+"F9.wireOp",EDGE,"E80"),sQuery(id+"F9.wireOp",EDGE,"E81"),sQuery(id+"F9.wireOp",EDGE,"E82"),sQuery(id+"F9.wireOp",EDGE,"E83"),sQuery(id+"F9.wireOp",EDGE,"E84")])]}),makeQuery(id+"F17.opExtrude","SWEPT_BODY",BODY,{"disambiguationData":[OSD([sQuery(id+"F14.wireOp",EDGE,"E124"),sQuery(id+"F14.wireOp",EDGE,"E125"),sQuery(id+"F14.wireOp",EDGE,"E128"),sQuery(id+"F14.wireOp",EDGE,"E133"),sQuery(id+"F14.wireOp",EDGE,"E134"),sQuery(id+"F14.wireOp",EDGE,"E135")])]})]});
            booleanBodies(context, id + "F30", {"operationType" : BooleanOperationType.SUBTRACTION, "tools" : qUnion([Q0]), "targets" : qUnion([Q1])});
        }
        {
            var Q0;
            Q0=qCreatedBy(makeId("Front.planeOp"),FACE);
            var sketch = newSketch(context, id + "F31", { "sketchPlane" : qUnion([Q0])});
            skLineSegment(sketch, "E160.0", {"start": v(15.5, 97.2) * mm, "end": v(15.5, 118) * mm});
            skLineSegment(sketch, "E161.0", {"start": v(16.7, -1) * mm, "end": v(16.7, 96) * mm});
            skLineSegment(sketch, "E162", {"start": v(15.5, 118) * mm, "end": v(41.7, 118) * mm});
            skLineSegment(sketch, "E163", {"start": v(41.7, 118) * mm, "end": v(41.7, -11) * mm});
            skLineSegment(sketch, "E164", {"start": v(41.7, -11) * mm, "end": v(16.7, -11) * mm});
            skLineSegment(sketch, "E165", {"start": v(16.7, -11) * mm, "end": v(16.7, -1) * mm});
            skLineSegment(sketch, "E166", {"start": v(5, 118) * mm, "end": v(5, -11) * mm, "construction": true});
            skPoint(sketch, "E167.0.end.orphan", {"position": v(15.5, 97.2) * mm});
            skLineSegment(sketch, "E168", {"start": v(15.5, 97.2) * mm, "end": v(16.7, 96) * mm});
            skSolve(sketch);
        }
        {
            var Q0;
            Q0=qCreatedBy(makeId("Front.planeOp"),FACE);
            var sketch = newSketch(context, id + "F32", { "sketchPlane" : qUnion([Q0])});
            skLineSegment(sketch, "E169.0", {"start": v(16.3, 98) * mm, "end": v(16.3, 118) * mm});
            skLineSegment(sketch, "E169.1", {"start": v(41.7, 118) * mm, "end": v(41.7, -11) * mm});
            skLineSegment(sketch, "E169.2", {"start": v(17.5, -2) * mm, "end": v(17.5, 98) * mm});
            skLineSegment(sketch, "E169.3", {"start": v(17.5, 98) * mm, "end": v(16.3, 98) * mm});
            skLineSegment(sketch, "E170", {"start": v(16.3, 118) * mm, "end": v(41.7, 118) * mm});
            skLineSegment(sketch, "E171", {"start": v(17.5, -2) * mm, "end": v(17.5, -11) * mm});
            skLineSegment(sketch, "E172", {"start": v(17.5, -11) * mm, "end": v(41.7, -11) * mm});
            skSolve(sketch);
        }
        {
            var Q0;
            Q0 = qSketchRegion(id + "F31", true);
            var Q1;
            Q1 = qSketchRegion(id + "F32", true);
            var Q2;
            Q2=sQuery(id+"F31.wireOp",EDGE,"E166");
            revolve(context, id + "F33", {"surfaceOperationType" : NewSurfaceOperationType.NEW, "entities" : qUnion([Q0, Q1]), "axis" : qUnion([Q2]), "revolveType" : RevolveType.ONE_DIRECTION, "angle" : 90 * degree});
        }
        {
            var Q0;
            Q0=makeQuery(id+"F33.opRevolve","SWEPT_BODY",BODY,{"disambiguationData":[OSD([sQuery(id+"F31.wireOp",EDGE,"E160.0"),sQuery(id+"F31.wireOp",EDGE,"E167.0"),sQuery(id+"F31.wireOp",EDGE,"E161.0"),sQuery(id+"F31.wireOp",EDGE,"E162"),sQuery(id+"F31.wireOp",EDGE,"E163"),sQuery(id+"F31.wireOp",EDGE,"E164"),sQuery(id+"F31.wireOp",EDGE,"E165")])]});
            var Q1;
            Q1=makeQuery(id+"F33.opRevolve","SWEPT_BODY",BODY,{"disambiguationData":[OSD([sQuery(id+"F32.wireOp",EDGE,"E169.0"),sQuery(id+"F32.wireOp",EDGE,"E169.1"),sQuery(id+"F32.wireOp",EDGE,"E169.2"),sQuery(id+"F32.wireOp",EDGE,"E169.3"),sQuery(id+"F32.wireOp",EDGE,"E170"),sQuery(id+"F32.wireOp",EDGE,"E171"),sQuery(id+"F32.wireOp",EDGE,"E172")])]});
            transform(context, id + "F34", {"entities" : qUnion([Q0, Q1]), "transformType" : TransformType.TRANSLATION_3D, "dx" : 0 * mm, "dy" : getVariable(context, 'Round_trans') * mm, "dz" : 0 * mm, "makeCopy" : false});
        }
        {
            var Q0;
            Q0=makeQuery(id+"F33.opRevolve","SWEPT_BODY",BODY,{"disambiguationData":[OSD([sQuery(id+"F31.wireOp",EDGE,"E160.0"),sQuery(id+"F31.wireOp",EDGE,"E167.0"),sQuery(id+"F31.wireOp",EDGE,"E161.0"),sQuery(id+"F31.wireOp",EDGE,"E162"),sQuery(id+"F31.wireOp",EDGE,"E163"),sQuery(id+"F31.wireOp",EDGE,"E164"),sQuery(id+"F31.wireOp",EDGE,"E165")])]});
            var Q1;
            Q1=makeQuery(id+"F33.opRevolve","SWEPT_BODY",BODY,{"disambiguationData":[OSD([sQuery(id+"F32.wireOp",EDGE,"E169.0"),sQuery(id+"F32.wireOp",EDGE,"E169.1"),sQuery(id+"F32.wireOp",EDGE,"E169.2"),sQuery(id+"F32.wireOp",EDGE,"E169.3"),sQuery(id+"F32.wireOp",EDGE,"E170"),sQuery(id+"F32.wireOp",EDGE,"E171"),sQuery(id+"F32.wireOp",EDGE,"E172")])]});
            var Q2;
            Q2=qCreatedBy(makeId("Right.planeOp"),FACE);
            mirror(context, id + "F35", {"entities" : qUnion([Q0, Q1]), "mirrorPlane" : qUnion([Q2])});
        }
        {
            var Q0;
            Q0=makeQuery(id+"F35.opPattern","COPY",BODY,{"derivedFrom":makeQuery(id+"F33.opRevolve","SWEPT_BODY",BODY,{"disambiguationData":[OSD([sQuery(id+"F31.wireOp",EDGE,"E160.0"),sQuery(id+"F31.wireOp",EDGE,"E167.0"),sQuery(id+"F31.wireOp",EDGE,"E161.0"),sQuery(id+"F31.wireOp",EDGE,"E162"),sQuery(id+"F31.wireOp",EDGE,"E163"),sQuery(id+"F31.wireOp",EDGE,"E164"),sQuery(id+"F31.wireOp",EDGE,"E165")])]}),"instanceName":"1"});
            var Q1;
            Q1=makeQuery(id+"F33.opRevolve","SWEPT_BODY",BODY,{"disambiguationData":[OSD([sQuery(id+"F31.wireOp",EDGE,"E160.0"),sQuery(id+"F31.wireOp",EDGE,"E167.0"),sQuery(id+"F31.wireOp",EDGE,"E161.0"),sQuery(id+"F31.wireOp",EDGE,"E162"),sQuery(id+"F31.wireOp",EDGE,"E163"),sQuery(id+"F31.wireOp",EDGE,"E164"),sQuery(id+"F31.wireOp",EDGE,"E165")])]});
            var Q2;
            Q2=makeQuery(id+"F21.opBoolean","INTERSECT",BODY,{"derivedFrom":[makeQuery(id+"F16.opExtrude","SWEPT_BODY",BODY,{"disambiguationData":[OSD([sQuery(id+"F8.wireOp",EDGE,"E68"),sQuery(id+"F8.wireOp",EDGE,"E69"),sQuery(id+"F8.wireOp",EDGE,"E70"),sQuery(id+"F8.wireOp",EDGE,"E71"),sQuery(id+"F8.wireOp",EDGE,"E72"),sQuery(id+"F8.wireOp",EDGE,"E73"),sQuery(id+"F8.wireOp",EDGE,"E74"),sQuery(id+"F8.wireOp",EDGE,"E75")])]}),makeQuery(id+"F17.opExtrude","SWEPT_BODY",BODY,{"disambiguationData":[OSD([sQuery(id+"F13.wireOp",EDGE,"E112"),sQuery(id+"F13.wireOp",EDGE,"E113"),sQuery(id+"F13.wireOp",EDGE,"E114"),sQuery(id+"F13.wireOp",EDGE,"E115"),sQuery(id+"F13.wireOp",EDGE,"E116"),sQuery(id+"F13.wireOp",EDGE,"E117"),sQuery(id+"F13.wireOp",EDGE,"E118"),sQuery(id+"F13.wireOp",EDGE,"E119")])]})]});
            booleanBodies(context, id + "F36", {"operationType" : BooleanOperationType.SUBTRACTION, "tools" : qUnion([Q0, Q1]), "targets" : qUnion([Q2])});
        }
        {
            var Q0;
            Q0=makeQuery(id+"F35.opPattern","COPY",BODY,{"derivedFrom":makeQuery(id+"F33.opRevolve","SWEPT_BODY",BODY,{"disambiguationData":[OSD([sQuery(id+"F32.wireOp",EDGE,"E169.0"),sQuery(id+"F32.wireOp",EDGE,"E169.1"),sQuery(id+"F32.wireOp",EDGE,"E169.2"),sQuery(id+"F32.wireOp",EDGE,"E169.3"),sQuery(id+"F32.wireOp",EDGE,"E170"),sQuery(id+"F32.wireOp",EDGE,"E171"),sQuery(id+"F32.wireOp",EDGE,"E172")])]}),"instanceName":"1"});
            var Q1;
            Q1=makeQuery(id+"F33.opRevolve","SWEPT_BODY",BODY,{"disambiguationData":[OSD([sQuery(id+"F32.wireOp",EDGE,"E169.0"),sQuery(id+"F32.wireOp",EDGE,"E169.1"),sQuery(id+"F32.wireOp",EDGE,"E169.2"),sQuery(id+"F32.wireOp",EDGE,"E169.3"),sQuery(id+"F32.wireOp",EDGE,"E170"),sQuery(id+"F32.wireOp",EDGE,"E171"),sQuery(id+"F32.wireOp",EDGE,"E172")])]});
            var Q2;
            Q2=makeQuery(id+"F20.opBoolean","INTERSECT",BODY,{"derivedFrom":[makeQuery(id+"F16.opExtrude","SWEPT_BODY",BODY,{"disambiguationData":[OSD([sQuery(id+"F7.wireOp",EDGE,"E60"),sQuery(id+"F7.wireOp",EDGE,"E61"),sQuery(id+"F7.wireOp",EDGE,"E62"),sQuery(id+"F7.wireOp",EDGE,"E63"),sQuery(id+"F7.wireOp",EDGE,"E64"),sQuery(id+"F7.wireOp",EDGE,"E65"),sQuery(id+"F7.wireOp",EDGE,"E66"),sQuery(id+"F7.wireOp",EDGE,"E67")])]}),makeQuery(id+"F17.opExtrude","SWEPT_BODY",BODY,{"disambiguationData":[OSD([sQuery(id+"F12.wireOp",EDGE,"E104"),sQuery(id+"F12.wireOp",EDGE,"E105"),sQuery(id+"F12.wireOp",EDGE,"E106"),sQuery(id+"F12.wireOp",EDGE,"E107"),sQuery(id+"F12.wireOp",EDGE,"E108"),sQuery(id+"F12.wireOp",EDGE,"E109"),sQuery(id+"F12.wireOp",EDGE,"E110"),sQuery(id+"F12.wireOp",EDGE,"E111")])]})]});
            booleanBodies(context, id + "F37", {"operationType" : BooleanOperationType.SUBTRACTION, "tools" : qUnion([Q0, Q1]), "targets" : qUnion([Q2])});
        }
        {
            var Q0;
            Q0=makeQuery(id+"F21.opBoolean","INTERSECT",BODY,{"derivedFrom":[makeQuery(id+"F16.opExtrude","SWEPT_BODY",BODY,{"disambiguationData":[OSD([sQuery(id+"F8.wireOp",EDGE,"E68"),sQuery(id+"F8.wireOp",EDGE,"E69"),sQuery(id+"F8.wireOp",EDGE,"E70"),sQuery(id+"F8.wireOp",EDGE,"E71"),sQuery(id+"F8.wireOp",EDGE,"E72"),sQuery(id+"F8.wireOp",EDGE,"E73"),sQuery(id+"F8.wireOp",EDGE,"E74"),sQuery(id+"F8.wireOp",EDGE,"E75")])]}),makeQuery(id+"F17.opExtrude","SWEPT_BODY",BODY,{"disambiguationData":[OSD([sQuery(id+"F13.wireOp",EDGE,"E112"),sQuery(id+"F13.wireOp",EDGE,"E113"),sQuery(id+"F13.wireOp",EDGE,"E114"),sQuery(id+"F13.wireOp",EDGE,"E115"),sQuery(id+"F13.wireOp",EDGE,"E116"),sQuery(id+"F13.wireOp",EDGE,"E117"),sQuery(id+"F13.wireOp",EDGE,"E118"),sQuery(id+"F13.wireOp",EDGE,"E119")])]})]});
            var Q1;
            Q1=makeQuery(id+"F20.opBoolean","INTERSECT",BODY,{"derivedFrom":[makeQuery(id+"F16.opExtrude","SWEPT_BODY",BODY,{"disambiguationData":[OSD([sQuery(id+"F7.wireOp",EDGE,"E60"),sQuery(id+"F7.wireOp",EDGE,"E61"),sQuery(id+"F7.wireOp",EDGE,"E62"),sQuery(id+"F7.wireOp",EDGE,"E63"),sQuery(id+"F7.wireOp",EDGE,"E64"),sQuery(id+"F7.wireOp",EDGE,"E65"),sQuery(id+"F7.wireOp",EDGE,"E66"),sQuery(id+"F7.wireOp",EDGE,"E67")])]}),makeQuery(id+"F17.opExtrude","SWEPT_BODY",BODY,{"disambiguationData":[OSD([sQuery(id+"F12.wireOp",EDGE,"E104"),sQuery(id+"F12.wireOp",EDGE,"E105"),sQuery(id+"F12.wireOp",EDGE,"E106"),sQuery(id+"F12.wireOp",EDGE,"E107"),sQuery(id+"F12.wireOp",EDGE,"E108"),sQuery(id+"F12.wireOp",EDGE,"E109"),sQuery(id+"F12.wireOp",EDGE,"E110"),sQuery(id+"F12.wireOp",EDGE,"E111")])]})]});
            booleanBodies(context, id + "F38", {"operationType" : BooleanOperationType.SUBTRACTION, "tools" : qUnion([Q0]), "targets" : qUnion([Q1])});
        }
        {
            var Q0;
            Q0=qCreatedBy(makeId("Front.planeOp"),FACE);
            var sketch = newSketch(context, id + "F39", { "sketchPlane" : qUnion([Q0])});
            skLineSegment(sketch, "E173.bottom", {"start": v(15.5, 118) * mm, "end": v(16.3, 118) * mm});
            skLineSegment(sketch, "E173.top", {"start": v(15.5, 78) * mm, "end": v(17.5, 78) * mm});
            skLineSegment(sketch, "E173.left", {"start": v(15.5, 118) * mm, "end": v(15.5, 78) * mm});
            skLineSegment(sketch, "E173.right", {"start": v(17.5, 98) * mm, "end": v(17.5, 78) * mm});
            skLineSegment(sketch, "E174", {"start": v(16.3, 118) * mm, "end": v(16.3, 118) * mm});
            skLineSegment(sketch, "E175", {"start": v(16.3, 118) * mm, "end": v(18.3, 116) * mm});
            skLineSegment(sketch, "E176", {"start": v(18.3, 116) * mm, "end": v(16.3, 114) * mm});
            skLineSegment(sketch, "E177", {"start": v(16.3, 114) * mm, "end": v(16.3, 112) * mm});
            skLineSegment(sketch, "E178", {"start": v(16.3, 98) * mm, "end": v(17.5, 98) * mm});
            skLineSegment(sketch, "E179", {"start": v(16.3, 112) * mm, "end": v(18.3, 110) * mm});
            skLineSegment(sketch, "E180", {"start": v(18.3, 110) * mm, "end": v(16.3, 108) * mm});
            skLineSegment(sketch, "E181.trimOffspring", {"start": v(16.3, 108) * mm, "end": v(16.3, 98) * mm});
            skSolve(sketch);
        }
        {
            var Q0;
            Q0=qCreatedBy(makeId("Front.planeOp"),FACE);
            var sketch = newSketch(context, id + "F40", { "sketchPlane" : qUnion([Q0])});
            skLineSegment(sketch, "E182.0", {"start": v(16.3, 114) * mm, "end": v(16.3, 112) * mm});
            skLineSegment(sketch, "E182.1", {"start": v(16.3, 98) * mm, "end": v(17.5, 98) * mm});
            skLineSegment(sketch, "E182.3", {"start": v(16.3, 112) * mm, "end": v(18.3, 110) * mm});
            skLineSegment(sketch, "E182.5", {"start": v(15.5, 118) * mm, "end": v(16.3, 118) * mm});
            skLineSegment(sketch, "E182.6", {"start": v(18.3, 110) * mm, "end": v(16.3, 108) * mm});
            skLineSegment(sketch, "E182.8", {"start": v(16.3, 118) * mm, "end": v(18.3, 116) * mm});
            skLineSegment(sketch, "E182.9", {"start": v(18.3, 116) * mm, "end": v(16.3, 114) * mm});
            skLineSegment(sketch, "E182.10", {"start": v(15.5, 97.2) * mm, "end": v(15.5, 118) * mm});
            skLineSegment(sketch, "E183", {"start": v(16.3, 108) * mm, "end": v(16.3, 98) * mm});
            skLineSegment(sketch, "E184", {"start": v(17.5, 78) * mm, "end": v(16.7, 78) * mm});
            skLineSegment(sketch, "E185", {"start": v(16.7, 78) * mm, "end": v(16.7, 79) * mm});
            skLineSegment(sketch, "E186", {"start": v(16.7, 79) * mm, "end": v(17.2, 79.5) * mm});
            skLineSegment(sketch, "E187", {"start": v(17.2, 79.5) * mm, "end": v(16.7, 80) * mm});
            skLineSegment(sketch, "E188", {"start": v(16.7, 80) * mm, "end": v(17.2, 80.5) * mm});
            skLineSegment(sketch, "E189", {"start": v(17.2, 80.5) * mm, "end": v(16.7, 81) * mm});
            skLineSegment(sketch, "E190", {"start": v(16.7, 81) * mm, "end": v(16.7, 82.39) * mm});
            skLineSegment(sketch, "E191", {"start": v(16.7, 82.39) * mm, "end": v(15.5, 83.59) * mm});
            skLineSegment(sketch, "E192", {"start": v(15.5, 83.59) * mm, "end": v(15.5, 97.2) * mm});
            skLineSegment(sketch, "E193", {"start": v(17.5, 78) * mm, "end": v(17.5, 83) * mm});
            skLineSegment(sketch, "E194", {"start": v(17.5, 83) * mm, "end": v(16.7, 83.8) * mm});
            skLineSegment(sketch, "E195", {"start": v(16.7, 83.8) * mm, "end": v(16.7, 86.8) * mm});
            skLineSegment(sketch, "E196", {"start": v(16.7, 86.8) * mm, "end": v(17.5, 87.6) * mm});
            skLineSegment(sketch, "E197", {"start": v(17.5, 87.6) * mm, "end": v(17.5, 92.6) * mm});
            skLineSegment(sketch, "E198", {"start": v(17.5, 92.6) * mm, "end": v(16.7, 93.4) * mm});
            skLineSegment(sketch, "E199", {"start": v(16.7, 93.4) * mm, "end": v(16.7, 96.4) * mm});
            skLineSegment(sketch, "E200", {"start": v(16.7, 96.4) * mm, "end": v(17.5, 97.2) * mm});
            skLineSegment(sketch, "E201", {"start": v(17.5, 97.2) * mm, "end": v(17.5, 98) * mm});
            skSolve(sketch);
        }
        {
            var Q0;
            Q0 = qSketchRegion(id + "F39", true);
            extrude(context, id + "F41", {"entities" : qUnion([Q0]), "endBound" : BoundingType.SYMMETRIC, "depth" : 15 * mm, "offsetDistance" : 25 * mm});
        }
        {
            var Q0;
            Q0 = qSketchRegion(id + "F40", true);
            extrude(context, id + "F42", {"entities" : qUnion([Q0]), "endBound" : BoundingType.SYMMETRIC, "depth" : 14 * mm, "offsetDistance" : 25 * mm});
        }
        {
            var Q0;
            Q0=makeQuery(id+"F41.opExtrude","SWEPT_BODY",BODY,{"disambiguationData":[OSD([sQuery(id+"F39.wireOp",EDGE,"E173.bottom"),sQuery(id+"F39.wireOp",EDGE,"E173.top"),sQuery(id+"F39.wireOp",EDGE,"E173.left"),sQuery(id+"F39.wireOp",EDGE,"E173.right"),sQuery(id+"F39.wireOp",EDGE,"E174"),sQuery(id+"F39.wireOp",EDGE,"E175"),sQuery(id+"F39.wireOp",EDGE,"E176"),sQuery(id+"F39.wireOp",EDGE,"E177"),sQuery(id+"F39.wireOp",EDGE,"E178"),sQuery(id+"F39.wireOp",EDGE,"E179"),sQuery(id+"F39.wireOp",EDGE,"E180"),sQuery(id+"F39.wireOp",EDGE,"E181.trimOffspring")])]});
            var Q1;
            Q1=makeQuery(id+"F42.opExtrude","SWEPT_BODY",BODY,{"disambiguationData":[OSD([sQuery(id+"F40.wireOp",EDGE,"E182.0"),sQuery(id+"F40.wireOp",EDGE,"E182.1"),sQuery(id+"F40.wireOp",EDGE,"E182.3"),sQuery(id+"F40.wireOp",EDGE,"E182.4"),sQuery(id+"F40.wireOp",EDGE,"E182.5"),sQuery(id+"F40.wireOp",EDGE,"E182.6"),sQuery(id+"F40.wireOp",EDGE,"E182.8"),sQuery(id+"F40.wireOp",EDGE,"E182.9"),sQuery(id+"F40.wireOp",EDGE,"E182.10"),sQuery(id+"F40.wireOp",EDGE,"E183"),sQuery(id+"F40.wireOp",EDGE,"E184"),sQuery(id+"F40.wireOp",EDGE,"E185"),sQuery(id+"F40.wireOp",EDGE,"E186"),sQuery(id+"F40.wireOp",EDGE,"E187"),sQuery(id+"F40.wireOp",EDGE,"E188"),sQuery(id+"F40.wireOp",EDGE,"E189"),sQuery(id+"F40.wireOp",EDGE,"E190"),sQuery(id+"F40.wireOp",EDGE,"E191"),sQuery(id+"F40.wireOp",EDGE,"E192"),sQuery(id+"F40.wireOp",EDGE,"E193"),sQuery(id+"F40.wireOp",EDGE,"E194"),sQuery(id+"F40.wireOp",EDGE,"E195"),sQuery(id+"F40.wireOp",EDGE,"E196"),sQuery(id+"F40.wireOp",EDGE,"E197"),sQuery(id+"F40.wireOp",EDGE,"E198"),sQuery(id+"F40.wireOp",EDGE,"E199"),sQuery(id+"F40.wireOp",EDGE,"E200"),sQuery(id+"F40.wireOp",EDGE,"E201")])]});
            transform(context, id + "F43", {"entities" : qUnion([Q0, Q1]), "transformType" : TransformType.TRANSLATION_3D, "dx" : 0 * mm, "dy" : 18 * mm, "dz" : 0 * mm, "makeCopy" : false});
        }
        {
            var Q0;
            Q0=makeQuery(id+"F41.opExtrude","SWEPT_BODY",BODY,{"disambiguationData":[OSD([sQuery(id+"F39.wireOp",EDGE,"E173.bottom"),sQuery(id+"F39.wireOp",EDGE,"E173.top"),sQuery(id+"F39.wireOp",EDGE,"E173.left"),sQuery(id+"F39.wireOp",EDGE,"E173.right"),sQuery(id+"F39.wireOp",EDGE,"E174"),sQuery(id+"F39.wireOp",EDGE,"E175"),sQuery(id+"F39.wireOp",EDGE,"E176"),sQuery(id+"F39.wireOp",EDGE,"E177"),sQuery(id+"F39.wireOp",EDGE,"E178"),sQuery(id+"F39.wireOp",EDGE,"E179"),sQuery(id+"F39.wireOp",EDGE,"E180"),sQuery(id+"F39.wireOp",EDGE,"E181.trimOffspring")])]});
            var Q1;
            Q1=makeQuery(id+"F42.opExtrude","SWEPT_BODY",BODY,{"disambiguationData":[OSD([sQuery(id+"F40.wireOp",EDGE,"E182.0"),sQuery(id+"F40.wireOp",EDGE,"E182.1"),sQuery(id+"F40.wireOp",EDGE,"E182.3"),sQuery(id+"F40.wireOp",EDGE,"E182.4"),sQuery(id+"F40.wireOp",EDGE,"E182.5"),sQuery(id+"F40.wireOp",EDGE,"E182.6"),sQuery(id+"F40.wireOp",EDGE,"E182.8"),sQuery(id+"F40.wireOp",EDGE,"E182.9"),sQuery(id+"F40.wireOp",EDGE,"E182.10"),sQuery(id+"F40.wireOp",EDGE,"E183"),sQuery(id+"F40.wireOp",EDGE,"E184"),sQuery(id+"F40.wireOp",EDGE,"E185"),sQuery(id+"F40.wireOp",EDGE,"E186"),sQuery(id+"F40.wireOp",EDGE,"E187"),sQuery(id+"F40.wireOp",EDGE,"E188"),sQuery(id+"F40.wireOp",EDGE,"E189"),sQuery(id+"F40.wireOp",EDGE,"E190"),sQuery(id+"F40.wireOp",EDGE,"E191"),sQuery(id+"F40.wireOp",EDGE,"E192"),sQuery(id+"F40.wireOp",EDGE,"E193"),sQuery(id+"F40.wireOp",EDGE,"E194"),sQuery(id+"F40.wireOp",EDGE,"E195"),sQuery(id+"F40.wireOp",EDGE,"E196"),sQuery(id+"F40.wireOp",EDGE,"E197"),sQuery(id+"F40.wireOp",EDGE,"E198"),sQuery(id+"F40.wireOp",EDGE,"E199"),sQuery(id+"F40.wireOp",EDGE,"E200"),sQuery(id+"F40.wireOp",EDGE,"E201")])]});
            var Q2;
            Q2=qCreatedBy(makeId("Right.planeOp"),FACE);
            mirror(context, id + "F44", {"entities" : qUnion([Q0, Q1]), "mirrorPlane" : qUnion([Q2])});
        }
        {
            var Q0;
            Q0=makeQuery(id+"F44.opPattern","COPY",BODY,{"derivedFrom":makeQuery(id+"F41.opExtrude","SWEPT_BODY",BODY,{"disambiguationData":[OSD([sQuery(id+"F39.wireOp",EDGE,"E173.bottom"),sQuery(id+"F39.wireOp",EDGE,"E173.top"),sQuery(id+"F39.wireOp",EDGE,"E173.left"),sQuery(id+"F39.wireOp",EDGE,"E173.right"),sQuery(id+"F39.wireOp",EDGE,"E174"),sQuery(id+"F39.wireOp",EDGE,"E175"),sQuery(id+"F39.wireOp",EDGE,"E176"),sQuery(id+"F39.wireOp",EDGE,"E177"),sQuery(id+"F39.wireOp",EDGE,"E178"),sQuery(id+"F39.wireOp",EDGE,"E179"),sQuery(id+"F39.wireOp",EDGE,"E180"),sQuery(id+"F39.wireOp",EDGE,"E181.trimOffspring")])]}),"instanceName":"1"});
            var Q1;
            Q1=makeQuery(id+"F41.opExtrude","SWEPT_BODY",BODY,{"disambiguationData":[OSD([sQuery(id+"F39.wireOp",EDGE,"E173.bottom"),sQuery(id+"F39.wireOp",EDGE,"E173.top"),sQuery(id+"F39.wireOp",EDGE,"E173.left"),sQuery(id+"F39.wireOp",EDGE,"E173.right"),sQuery(id+"F39.wireOp",EDGE,"E174"),sQuery(id+"F39.wireOp",EDGE,"E175"),sQuery(id+"F39.wireOp",EDGE,"E176"),sQuery(id+"F39.wireOp",EDGE,"E177"),sQuery(id+"F39.wireOp",EDGE,"E178"),sQuery(id+"F39.wireOp",EDGE,"E179"),sQuery(id+"F39.wireOp",EDGE,"E180"),sQuery(id+"F39.wireOp",EDGE,"E181.trimOffspring")])]});
            var Q2;
            Q2=makeQuery(id+"F18.opBoolean","INTERSECT",BODY,{"derivedFrom":[makeQuery(id+"F16.opExtrude","SWEPT_BODY",BODY,{"disambiguationData":[OSD([sQuery(id+"F9.wireOp",EDGE,"E80"),sQuery(id+"F9.wireOp",EDGE,"E81"),sQuery(id+"F9.wireOp",EDGE,"E82"),sQuery(id+"F9.wireOp",EDGE,"E83"),sQuery(id+"F9.wireOp",EDGE,"E84")])]}),makeQuery(id+"F17.opExtrude","SWEPT_BODY",BODY,{"disambiguationData":[OSD([sQuery(id+"F14.wireOp",EDGE,"E124"),sQuery(id+"F14.wireOp",EDGE,"E125"),sQuery(id+"F14.wireOp",EDGE,"E128"),sQuery(id+"F14.wireOp",EDGE,"E133"),sQuery(id+"F14.wireOp",EDGE,"E134"),sQuery(id+"F14.wireOp",EDGE,"E135")])]})]});
            var Q3;
            Q3=makeQuery(id+"F20.opBoolean","INTERSECT",BODY,{"derivedFrom":[makeQuery(id+"F16.opExtrude","SWEPT_BODY",BODY,{"disambiguationData":[OSD([sQuery(id+"F7.wireOp",EDGE,"E60"),sQuery(id+"F7.wireOp",EDGE,"E61"),sQuery(id+"F7.wireOp",EDGE,"E62"),sQuery(id+"F7.wireOp",EDGE,"E63"),sQuery(id+"F7.wireOp",EDGE,"E64"),sQuery(id+"F7.wireOp",EDGE,"E65"),sQuery(id+"F7.wireOp",EDGE,"E66"),sQuery(id+"F7.wireOp",EDGE,"E67")])]}),makeQuery(id+"F17.opExtrude","SWEPT_BODY",BODY,{"disambiguationData":[OSD([sQuery(id+"F12.wireOp",EDGE,"E104"),sQuery(id+"F12.wireOp",EDGE,"E105"),sQuery(id+"F12.wireOp",EDGE,"E106"),sQuery(id+"F12.wireOp",EDGE,"E107"),sQuery(id+"F12.wireOp",EDGE,"E108"),sQuery(id+"F12.wireOp",EDGE,"E109"),sQuery(id+"F12.wireOp",EDGE,"E110"),sQuery(id+"F12.wireOp",EDGE,"E111")])]})]});
            booleanBodies(context, id + "F45", {"operationType" : BooleanOperationType.SUBTRACTION, "tools" : qUnion([Q0, Q1]), "targets" : qUnion([Q2, Q3])});
        }
        {
            var Q0;
            Q0=makeQuery(id+"F42.opExtrude","CAP_EDGE",EDGE,{"disambiguationData":[OSD([sQuery(id+"F40.wireOp",EDGE,"E197")])],"isStart":true});
            var Q1;
            Q1=makeQuery(id+"F42.opExtrude","CAP_EDGE",EDGE,{"disambiguationData":[OSD([sQuery(id+"F40.wireOp",EDGE,"E197")])],"isStart":false});
            chamfer(context, id + "F46", {"entities" : qUnion([Q0, Q1]), "width" : 1 * mm, "tangentPropagation" : true});
        }
        {
            var Q0;
            Q0=qCreatedBy(makeId("Right.planeOp"),FACE);
            var sketch = newSketch(context, id + "F47", { "sketchPlane" : qUnion([Q0])});
            skText(sketch, "E202", { "text": "KIMBERLY", "fontName": "OpenSans-Bold.ttf"});
            const initialGuessF47  = {"E202": [0, -0.005, 1, 0, 0.01]};
            skSetInitialGuess(sketch, initialGuessF47);
            skSolve(sketch);
        }
        {
            var Q0;
            Q0 = qSketchRegion(id + "F47", true);
            extrude(context, id + "F48", {"entities" : qUnion([Q0]), "depth" : 0.4 * mm, "offsetDistance" : 25 * mm});
        }
        {
            var Q0;
            Q0=qCreatedBy(makeId("Right.planeOp"),FACE);
            var sketch = newSketch(context, id + "F49", { "sketchPlane" : qUnion([Q0])});
            skLineSegment(sketch, "E203.bottom", {"start": v(0, 0) * mm, "end": v(33.82, 0) * mm});
            skLineSegment(sketch, "E203.top", {"start": v(0, 50.6) * mm, "end": v(33.82, 50.6) * mm});
            skLineSegment(sketch, "E203.left", {"start": v(0, 0) * mm, "end": v(0, 50.6) * mm});
            skLineSegment(sketch, "E203.right", {"start": v(33.82, 0) * mm, "end": v(33.82, 50.6) * mm});
            skSolve(sketch);
        }
        {
            var Q0;
            Q0 = qSketchRegion(id + "F49", true);
            extrude(context, id + "F50", {"entities" : qUnion([Q0]), "depth" : 25 * mm, "offsetDistance" : 25 * mm});
        }
        {
            var Q0;
            Q0=makeQuery(id+"F48.opExtrude","SWEPT_BODY",BODY,{"disambiguationData":[OSD([sQuery(id+"F47.wireOp",EDGE,"E202.sketch_text.stroke-0"),sQuery(id+"F47.wireOp",EDGE,"E202.sketch_text.stroke-1"),sQuery(id+"F47.wireOp",EDGE,"E202.sketch_text.stroke-2"),sQuery(id+"F47.wireOp",EDGE,"E202.sketch_text.stroke-3"),sQuery(id+"F47.wireOp",EDGE,"E202.sketch_text.stroke-4"),sQuery(id+"F47.wireOp",EDGE,"E202.sketch_text.stroke-5"),sQuery(id+"F47.wireOp",EDGE,"E202.sketch_text.stroke-6"),sQuery(id+"F47.wireOp",EDGE,"E202.sketch_text.stroke-7"),sQuery(id+"F47.wireOp",EDGE,"E202.sketch_text.stroke-8"),sQuery(id+"F47.wireOp",EDGE,"E202.sketch_text.stroke-9"),sQuery(id+"F47.wireOp",EDGE,"E202.sketch_text.stroke-10"),sQuery(id+"F47.wireOp",EDGE,"E202.sketch_text.stroke-11"),sQuery(id+"F47.wireOp",EDGE,"E202.sketch_text.stroke-12")])]});
            var Q1;
            Q1=makeQuery(id+"F48.opExtrude","SWEPT_BODY",BODY,{"disambiguationData":[OSD([sQuery(id+"F47.wireOp",EDGE,"E202.sketch_text.stroke-13"),sQuery(id+"F47.wireOp",EDGE,"E202.sketch_text.stroke-14"),sQuery(id+"F47.wireOp",EDGE,"E202.sketch_text.stroke-15"),sQuery(id+"F47.wireOp",EDGE,"E202.sketch_text.stroke-16")])]});
            var Q2;
            Q2=makeQuery(id+"F48.opExtrude","SWEPT_BODY",BODY,{"disambiguationData":[OSD([sQuery(id+"F47.wireOp",EDGE,"E202.sketch_text.stroke-17"),sQuery(id+"F47.wireOp",EDGE,"E202.sketch_text.stroke-18"),sQuery(id+"F47.wireOp",EDGE,"E202.sketch_text.stroke-19"),sQuery(id+"F47.wireOp",EDGE,"E202.sketch_text.stroke-20"),sQuery(id+"F47.wireOp",EDGE,"E202.sketch_text.stroke-21"),sQuery(id+"F47.wireOp",EDGE,"E202.sketch_text.stroke-22"),sQuery(id+"F47.wireOp",EDGE,"E202.sketch_text.stroke-23"),sQuery(id+"F47.wireOp",EDGE,"E202.sketch_text.stroke-24"),sQuery(id+"F47.wireOp",EDGE,"E202.sketch_text.stroke-25"),sQuery(id+"F47.wireOp",EDGE,"E202.sketch_text.stroke-26"),sQuery(id+"F47.wireOp",EDGE,"E202.sketch_text.stroke-27"),sQuery(id+"F47.wireOp",EDGE,"E202.sketch_text.stroke-28"),sQuery(id+"F47.wireOp",EDGE,"E202.sketch_text.stroke-29"),sQuery(id+"F47.wireOp",EDGE,"E202.sketch_text.stroke-30"),sQuery(id+"F47.wireOp",EDGE,"E202.sketch_text.stroke-31"),sQuery(id+"F47.wireOp",EDGE,"E202.sketch_text.stroke-32"),sQuery(id+"F47.wireOp",EDGE,"E202.sketch_text.stroke-33"),sQuery(id+"F47.wireOp",EDGE,"E202.sketch_text.stroke-34"),sQuery(id+"F47.wireOp",EDGE,"E202.sketch_text.stroke-35")])]});
            var Q3;
            Q3=makeQuery(id+"F48.opExtrude","SWEPT_BODY",BODY,{"disambiguationData":[OSD([sQuery(id+"F47.wireOp",EDGE,"E202.sketch_text.stroke-36"),sQuery(id+"F47.wireOp",EDGE,"E202.sketch_text.stroke-37"),sQuery(id+"F47.wireOp",EDGE,"E202.sketch_text.stroke-38"),sQuery(id+"F47.wireOp",EDGE,"E202.sketch_text.stroke-39"),sQuery(id+"F47.wireOp",EDGE,"E202.sketch_text.stroke-40"),sQuery(id+"F47.wireOp",EDGE,"E202.sketch_text.stroke-41"),sQuery(id+"F47.wireOp",EDGE,"E202.sketch_text.stroke-42"),sQuery(id+"F47.wireOp",EDGE,"E202.sketch_text.stroke-43"),sQuery(id+"F47.wireOp",EDGE,"E202.sketch_text.stroke-44"),sQuery(id+"F47.wireOp",EDGE,"E202.sketch_text.stroke-45"),sQuery(id+"F47.wireOp",EDGE,"E202.sketch_text.stroke-46"),sQuery(id+"F47.wireOp",EDGE,"E202.sketch_text.stroke-47"),sQuery(id+"F47.wireOp",EDGE,"E202.sketch_text.stroke-48"),sQuery(id+"F47.wireOp",EDGE,"E202.sketch_text.stroke-49"),sQuery(id+"F47.wireOp",EDGE,"E202.sketch_text.stroke-50"),sQuery(id+"F47.wireOp",EDGE,"E202.sketch_text.stroke-51"),sQuery(id+"F47.wireOp",EDGE,"E202.sketch_text.stroke-52"),sQuery(id+"F47.wireOp",EDGE,"E202.sketch_text.stroke-53"),sQuery(id+"F47.wireOp",EDGE,"E202.sketch_text.stroke-54"),sQuery(id+"F47.wireOp",EDGE,"E202.sketch_text.stroke-55"),sQuery(id+"F47.wireOp",EDGE,"E202.sketch_text.stroke-56"),sQuery(id+"F47.wireOp",EDGE,"E202.sketch_text.stroke-57"),sQuery(id+"F47.wireOp",EDGE,"E202.sketch_text.stroke-58"),sQuery(id+"F47.wireOp",EDGE,"E202.sketch_text.stroke-59"),sQuery(id+"F47.wireOp",EDGE,"E202.sketch_text.stroke-60")])]});
            var Q4;
            Q4=makeQuery(id+"F48.opExtrude","SWEPT_BODY",BODY,{"disambiguationData":[OSD([sQuery(id+"F47.wireOp",EDGE,"E202.sketch_text.stroke-61"),sQuery(id+"F47.wireOp",EDGE,"E202.sketch_text.stroke-62"),sQuery(id+"F47.wireOp",EDGE,"E202.sketch_text.stroke-63"),sQuery(id+"F47.wireOp",EDGE,"E202.sketch_text.stroke-64"),sQuery(id+"F47.wireOp",EDGE,"E202.sketch_text.stroke-65"),sQuery(id+"F47.wireOp",EDGE,"E202.sketch_text.stroke-66"),sQuery(id+"F47.wireOp",EDGE,"E202.sketch_text.stroke-67"),sQuery(id+"F47.wireOp",EDGE,"E202.sketch_text.stroke-68"),sQuery(id+"F47.wireOp",EDGE,"E202.sketch_text.stroke-69"),sQuery(id+"F47.wireOp",EDGE,"E202.sketch_text.stroke-70"),sQuery(id+"F47.wireOp",EDGE,"E202.sketch_text.stroke-71"),sQuery(id+"F47.wireOp",EDGE,"E202.sketch_text.stroke-72")])]});
            var Q5;
            Q5=makeQuery(id+"F48.opExtrude","SWEPT_BODY",BODY,{"disambiguationData":[OSD([sQuery(id+"F47.wireOp",EDGE,"E202.sketch_text.stroke-73"),sQuery(id+"F47.wireOp",EDGE,"E202.sketch_text.stroke-74"),sQuery(id+"F47.wireOp",EDGE,"E202.sketch_text.stroke-75"),sQuery(id+"F47.wireOp",EDGE,"E202.sketch_text.stroke-76"),sQuery(id+"F47.wireOp",EDGE,"E202.sketch_text.stroke-77"),sQuery(id+"F47.wireOp",EDGE,"E202.sketch_text.stroke-78"),sQuery(id+"F47.wireOp",EDGE,"E202.sketch_text.stroke-79"),sQuery(id+"F47.wireOp",EDGE,"E202.sketch_text.stroke-80"),sQuery(id+"F47.wireOp",EDGE,"E202.sketch_text.stroke-81"),sQuery(id+"F47.wireOp",EDGE,"E202.sketch_text.stroke-82"),sQuery(id+"F47.wireOp",EDGE,"E202.sketch_text.stroke-83"),sQuery(id+"F47.wireOp",EDGE,"E202.sketch_text.stroke-84"),sQuery(id+"F47.wireOp",EDGE,"E202.sketch_text.stroke-85"),sQuery(id+"F47.wireOp",EDGE,"E202.sketch_text.stroke-86"),sQuery(id+"F47.wireOp",EDGE,"E202.sketch_text.stroke-87"),sQuery(id+"F47.wireOp",EDGE,"E202.sketch_text.stroke-88"),sQuery(id+"F47.wireOp",EDGE,"E202.sketch_text.stroke-89"),sQuery(id+"F47.wireOp",EDGE,"E202.sketch_text.stroke-90"),sQuery(id+"F47.wireOp",EDGE,"E202.sketch_text.stroke-91")])]});
            var Q6;
            Q6=makeQuery(id+"F48.opExtrude","SWEPT_BODY",BODY,{"disambiguationData":[OSD([sQuery(id+"F47.wireOp",EDGE,"E202.sketch_text.stroke-92"),sQuery(id+"F47.wireOp",EDGE,"E202.sketch_text.stroke-93"),sQuery(id+"F47.wireOp",EDGE,"E202.sketch_text.stroke-94"),sQuery(id+"F47.wireOp",EDGE,"E202.sketch_text.stroke-95"),sQuery(id+"F47.wireOp",EDGE,"E202.sketch_text.stroke-96"),sQuery(id+"F47.wireOp",EDGE,"E202.sketch_text.stroke-97")])]});
            var Q7;
            Q7=makeQuery(id+"F48.opExtrude","SWEPT_BODY",BODY,{"disambiguationData":[OSD([sQuery(id+"F47.wireOp",EDGE,"E202.sketch_text.stroke-98"),sQuery(id+"F47.wireOp",EDGE,"E202.sketch_text.stroke-99"),sQuery(id+"F47.wireOp",EDGE,"E202.sketch_text.stroke-100"),sQuery(id+"F47.wireOp",EDGE,"E202.sketch_text.stroke-101"),sQuery(id+"F47.wireOp",EDGE,"E202.sketch_text.stroke-102"),sQuery(id+"F47.wireOp",EDGE,"E202.sketch_text.stroke-103"),sQuery(id+"F47.wireOp",EDGE,"E202.sketch_text.stroke-104"),sQuery(id+"F47.wireOp",EDGE,"E202.sketch_text.stroke-105"),sQuery(id+"F47.wireOp",EDGE,"E202.sketch_text.stroke-106")])]});
            var Q8;
            Q8=makeQuery(id+"F50.opExtrude","SWEPT_EDGE",EDGE,{"disambiguationData":[OSD([sQuery(id+"F49.wireOp",EDGE,"E203.bottom"),sQuery(id+"F49.wireOp",EDGE,"E203.left")])]});
            transform(context, id + "F51", {"entities" : qUnion([Q0, Q1, Q2, Q3, Q4, Q5, Q6, Q7]), "transformType" : TransformType.ROTATION, "transformAxis" : qUnion([Q8]), "angle" : 90 * degree, "makeCopy" : false});
        }
        {
            var Q0;
            Q0=makeQuery(id+"F48.opExtrude","SWEPT_BODY",BODY,{"disambiguationData":[OSD([sQuery(id+"F47.wireOp",EDGE,"E202.sketch_text.stroke-0"),sQuery(id+"F47.wireOp",EDGE,"E202.sketch_text.stroke-1"),sQuery(id+"F47.wireOp",EDGE,"E202.sketch_text.stroke-2"),sQuery(id+"F47.wireOp",EDGE,"E202.sketch_text.stroke-3"),sQuery(id+"F47.wireOp",EDGE,"E202.sketch_text.stroke-4"),sQuery(id+"F47.wireOp",EDGE,"E202.sketch_text.stroke-5"),sQuery(id+"F47.wireOp",EDGE,"E202.sketch_text.stroke-6"),sQuery(id+"F47.wireOp",EDGE,"E202.sketch_text.stroke-7"),sQuery(id+"F47.wireOp",EDGE,"E202.sketch_text.stroke-8"),sQuery(id+"F47.wireOp",EDGE,"E202.sketch_text.stroke-9"),sQuery(id+"F47.wireOp",EDGE,"E202.sketch_text.stroke-10"),sQuery(id+"F47.wireOp",EDGE,"E202.sketch_text.stroke-11"),sQuery(id+"F47.wireOp",EDGE,"E202.sketch_text.stroke-12")])]});
            var Q1;
            Q1=makeQuery(id+"F48.opExtrude","SWEPT_BODY",BODY,{"disambiguationData":[OSD([sQuery(id+"F47.wireOp",EDGE,"E202.sketch_text.stroke-13"),sQuery(id+"F47.wireOp",EDGE,"E202.sketch_text.stroke-14"),sQuery(id+"F47.wireOp",EDGE,"E202.sketch_text.stroke-15"),sQuery(id+"F47.wireOp",EDGE,"E202.sketch_text.stroke-16")])]});
            var Q2;
            Q2=makeQuery(id+"F48.opExtrude","SWEPT_BODY",BODY,{"disambiguationData":[OSD([sQuery(id+"F47.wireOp",EDGE,"E202.sketch_text.stroke-17"),sQuery(id+"F47.wireOp",EDGE,"E202.sketch_text.stroke-18"),sQuery(id+"F47.wireOp",EDGE,"E202.sketch_text.stroke-19"),sQuery(id+"F47.wireOp",EDGE,"E202.sketch_text.stroke-20"),sQuery(id+"F47.wireOp",EDGE,"E202.sketch_text.stroke-21"),sQuery(id+"F47.wireOp",EDGE,"E202.sketch_text.stroke-22"),sQuery(id+"F47.wireOp",EDGE,"E202.sketch_text.stroke-23"),sQuery(id+"F47.wireOp",EDGE,"E202.sketch_text.stroke-24"),sQuery(id+"F47.wireOp",EDGE,"E202.sketch_text.stroke-25"),sQuery(id+"F47.wireOp",EDGE,"E202.sketch_text.stroke-26"),sQuery(id+"F47.wireOp",EDGE,"E202.sketch_text.stroke-27"),sQuery(id+"F47.wireOp",EDGE,"E202.sketch_text.stroke-28"),sQuery(id+"F47.wireOp",EDGE,"E202.sketch_text.stroke-29"),sQuery(id+"F47.wireOp",EDGE,"E202.sketch_text.stroke-30"),sQuery(id+"F47.wireOp",EDGE,"E202.sketch_text.stroke-31"),sQuery(id+"F47.wireOp",EDGE,"E202.sketch_text.stroke-32"),sQuery(id+"F47.wireOp",EDGE,"E202.sketch_text.stroke-33"),sQuery(id+"F47.wireOp",EDGE,"E202.sketch_text.stroke-34"),sQuery(id+"F47.wireOp",EDGE,"E202.sketch_text.stroke-35")])]});
            var Q3;
            Q3=makeQuery(id+"F48.opExtrude","SWEPT_BODY",BODY,{"disambiguationData":[OSD([sQuery(id+"F47.wireOp",EDGE,"E202.sketch_text.stroke-36"),sQuery(id+"F47.wireOp",EDGE,"E202.sketch_text.stroke-37"),sQuery(id+"F47.wireOp",EDGE,"E202.sketch_text.stroke-38"),sQuery(id+"F47.wireOp",EDGE,"E202.sketch_text.stroke-39"),sQuery(id+"F47.wireOp",EDGE,"E202.sketch_text.stroke-40"),sQuery(id+"F47.wireOp",EDGE,"E202.sketch_text.stroke-41"),sQuery(id+"F47.wireOp",EDGE,"E202.sketch_text.stroke-42"),sQuery(id+"F47.wireOp",EDGE,"E202.sketch_text.stroke-43"),sQuery(id+"F47.wireOp",EDGE,"E202.sketch_text.stroke-44"),sQuery(id+"F47.wireOp",EDGE,"E202.sketch_text.stroke-45"),sQuery(id+"F47.wireOp",EDGE,"E202.sketch_text.stroke-46"),sQuery(id+"F47.wireOp",EDGE,"E202.sketch_text.stroke-47"),sQuery(id+"F47.wireOp",EDGE,"E202.sketch_text.stroke-48"),sQuery(id+"F47.wireOp",EDGE,"E202.sketch_text.stroke-49"),sQuery(id+"F47.wireOp",EDGE,"E202.sketch_text.stroke-50"),sQuery(id+"F47.wireOp",EDGE,"E202.sketch_text.stroke-51"),sQuery(id+"F47.wireOp",EDGE,"E202.sketch_text.stroke-52"),sQuery(id+"F47.wireOp",EDGE,"E202.sketch_text.stroke-53"),sQuery(id+"F47.wireOp",EDGE,"E202.sketch_text.stroke-54"),sQuery(id+"F47.wireOp",EDGE,"E202.sketch_text.stroke-55"),sQuery(id+"F47.wireOp",EDGE,"E202.sketch_text.stroke-56"),sQuery(id+"F47.wireOp",EDGE,"E202.sketch_text.stroke-57"),sQuery(id+"F47.wireOp",EDGE,"E202.sketch_text.stroke-58"),sQuery(id+"F47.wireOp",EDGE,"E202.sketch_text.stroke-59"),sQuery(id+"F47.wireOp",EDGE,"E202.sketch_text.stroke-60")])]});
            var Q4;
            Q4=makeQuery(id+"F48.opExtrude","SWEPT_BODY",BODY,{"disambiguationData":[OSD([sQuery(id+"F47.wireOp",EDGE,"E202.sketch_text.stroke-61"),sQuery(id+"F47.wireOp",EDGE,"E202.sketch_text.stroke-62"),sQuery(id+"F47.wireOp",EDGE,"E202.sketch_text.stroke-63"),sQuery(id+"F47.wireOp",EDGE,"E202.sketch_text.stroke-64"),sQuery(id+"F47.wireOp",EDGE,"E202.sketch_text.stroke-65"),sQuery(id+"F47.wireOp",EDGE,"E202.sketch_text.stroke-66"),sQuery(id+"F47.wireOp",EDGE,"E202.sketch_text.stroke-67"),sQuery(id+"F47.wireOp",EDGE,"E202.sketch_text.stroke-68"),sQuery(id+"F47.wireOp",EDGE,"E202.sketch_text.stroke-69"),sQuery(id+"F47.wireOp",EDGE,"E202.sketch_text.stroke-70"),sQuery(id+"F47.wireOp",EDGE,"E202.sketch_text.stroke-71"),sQuery(id+"F47.wireOp",EDGE,"E202.sketch_text.stroke-72")])]});
            var Q5;
            Q5=makeQuery(id+"F48.opExtrude","SWEPT_BODY",BODY,{"disambiguationData":[OSD([sQuery(id+"F47.wireOp",EDGE,"E202.sketch_text.stroke-73"),sQuery(id+"F47.wireOp",EDGE,"E202.sketch_text.stroke-74"),sQuery(id+"F47.wireOp",EDGE,"E202.sketch_text.stroke-75"),sQuery(id+"F47.wireOp",EDGE,"E202.sketch_text.stroke-76"),sQuery(id+"F47.wireOp",EDGE,"E202.sketch_text.stroke-77"),sQuery(id+"F47.wireOp",EDGE,"E202.sketch_text.stroke-78"),sQuery(id+"F47.wireOp",EDGE,"E202.sketch_text.stroke-79"),sQuery(id+"F47.wireOp",EDGE,"E202.sketch_text.stroke-80"),sQuery(id+"F47.wireOp",EDGE,"E202.sketch_text.stroke-81"),sQuery(id+"F47.wireOp",EDGE,"E202.sketch_text.stroke-82"),sQuery(id+"F47.wireOp",EDGE,"E202.sketch_text.stroke-83"),sQuery(id+"F47.wireOp",EDGE,"E202.sketch_text.stroke-84"),sQuery(id+"F47.wireOp",EDGE,"E202.sketch_text.stroke-85"),sQuery(id+"F47.wireOp",EDGE,"E202.sketch_text.stroke-86"),sQuery(id+"F47.wireOp",EDGE,"E202.sketch_text.stroke-87"),sQuery(id+"F47.wireOp",EDGE,"E202.sketch_text.stroke-88"),sQuery(id+"F47.wireOp",EDGE,"E202.sketch_text.stroke-89"),sQuery(id+"F47.wireOp",EDGE,"E202.sketch_text.stroke-90"),sQuery(id+"F47.wireOp",EDGE,"E202.sketch_text.stroke-91")])]});
            var Q6;
            Q6=makeQuery(id+"F48.opExtrude","SWEPT_BODY",BODY,{"disambiguationData":[OSD([sQuery(id+"F47.wireOp",EDGE,"E202.sketch_text.stroke-92"),sQuery(id+"F47.wireOp",EDGE,"E202.sketch_text.stroke-93"),sQuery(id+"F47.wireOp",EDGE,"E202.sketch_text.stroke-94"),sQuery(id+"F47.wireOp",EDGE,"E202.sketch_text.stroke-95"),sQuery(id+"F47.wireOp",EDGE,"E202.sketch_text.stroke-96"),sQuery(id+"F47.wireOp",EDGE,"E202.sketch_text.stroke-97")])]});
            var Q7;
            Q7=makeQuery(id+"F48.opExtrude","SWEPT_BODY",BODY,{"disambiguationData":[OSD([sQuery(id+"F47.wireOp",EDGE,"E202.sketch_text.stroke-98"),sQuery(id+"F47.wireOp",EDGE,"E202.sketch_text.stroke-99"),sQuery(id+"F47.wireOp",EDGE,"E202.sketch_text.stroke-100"),sQuery(id+"F47.wireOp",EDGE,"E202.sketch_text.stroke-101"),sQuery(id+"F47.wireOp",EDGE,"E202.sketch_text.stroke-102"),sQuery(id+"F47.wireOp",EDGE,"E202.sketch_text.stroke-103"),sQuery(id+"F47.wireOp",EDGE,"E202.sketch_text.stroke-104"),sQuery(id+"F47.wireOp",EDGE,"E202.sketch_text.stroke-105"),sQuery(id+"F47.wireOp",EDGE,"E202.sketch_text.stroke-106")])]});
            transform(context, id + "F52", {"entities" : qUnion([Q0, Q1, Q2, Q3, Q4, Q5, Q6, Q7]), "transformType" : TransformType.TRANSLATION_3D, "dx" : 17.5 * mm, "dy" : 18 * mm, "dz" : 72.5 * mm, "makeCopy" : false});
        }
    });
